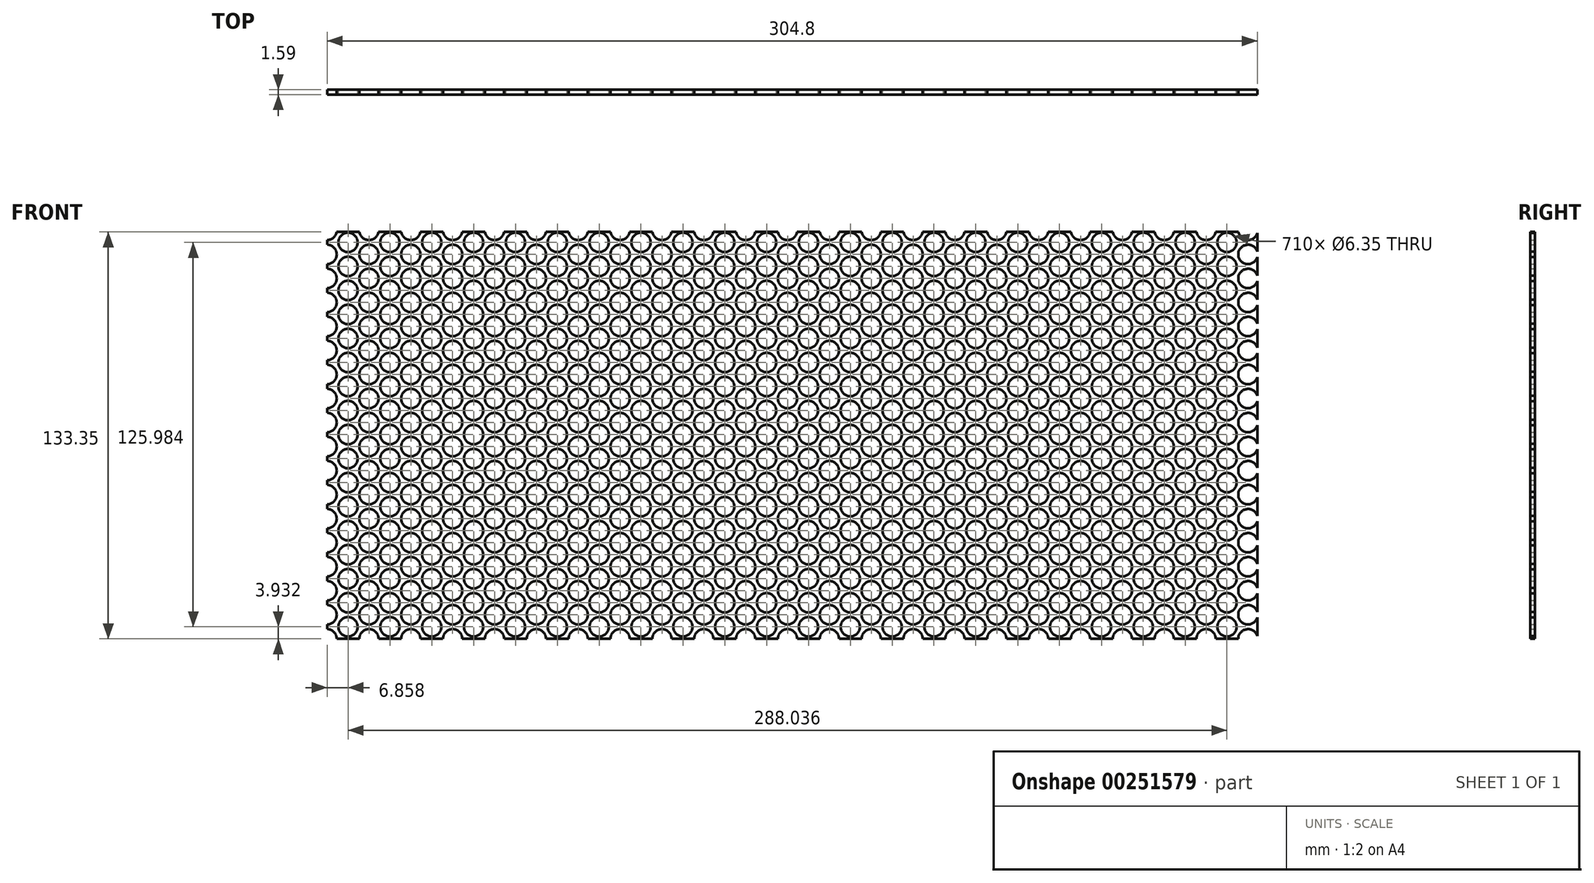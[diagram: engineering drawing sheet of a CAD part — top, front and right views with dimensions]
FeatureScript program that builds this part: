
annotation { "Feature Type Name" : "Feature", "Feature Type Description" : "" }
export const myFeature = defineFeature(function(context is Context, id is Id, definition is map)
    precondition{}
    {
        {
            var Q0;
            Q0=qCreatedBy(makeId("Front.planeOp"),FACE);
            var sketch = newSketch(context, id + "F0", { "sketchPlane" : qUnion([Q0])});
            skLineSegment(sketch, "E0.bottom", {"start": v(-127, 47.63) * mm, "end": v(177.8, 47.63) * mm});
            skLineSegment(sketch, "E0.top", {"start": v(-127, -85.73) * mm, "end": v(177.8, -85.73) * mm});
            skLineSegment(sketch, "E0.left", {"start": v(-127, 47.63) * mm, "end": v(-127, -85.73) * mm});
            skLineSegment(sketch, "E0.right", {"start": v(177.8, 47.63) * mm, "end": v(177.8, -85.73) * mm});
            skPoint(sketch, "E1", {"position": v(-127, -85.73) * mm});
            skPoint(sketch, "E2", {"position": v(-120.14, -81.79) * mm});
            skPoint(sketch, "E3.0.1.0", {"position": v(-127, -77.85) * mm});
            skPoint(sketch, "E3.0.1.1", {"position": v(-120.14, -73.91) * mm});
            skPoint(sketch, "E3.0.2.0", {"position": v(-127, -69.98) * mm});
            skPoint(sketch, "E3.0.2.1", {"position": v(-120.14, -66.04) * mm});
            skPoint(sketch, "E3.0.3.0", {"position": v(-127, -62.1) * mm});
            skPoint(sketch, "E3.0.3.1", {"position": v(-120.14, -58.17) * mm});
            skPoint(sketch, "E3.0.4.0", {"position": v(-127, -54.23) * mm});
            skPoint(sketch, "E3.0.4.1", {"position": v(-120.14, -50.3) * mm});
            skPoint(sketch, "E3.0.5.0", {"position": v(-127, -46.35) * mm});
            skPoint(sketch, "E3.0.5.1", {"position": v(-120.14, -42.42) * mm});
            skPoint(sketch, "E3.0.6.0", {"position": v(-127, -38.48) * mm});
            skPoint(sketch, "E3.0.6.1", {"position": v(-120.14, -34.54) * mm});
            skPoint(sketch, "E3.0.7.0", {"position": v(-127, -30.6) * mm});
            skPoint(sketch, "E3.0.7.1", {"position": v(-120.14, -26.67) * mm});
            skPoint(sketch, "E3.0.8.0", {"position": v(-127, -22.73) * mm});
            skPoint(sketch, "E3.0.8.1", {"position": v(-120.14, -18.8) * mm});
            skPoint(sketch, "E3.0.9.0", {"position": v(-127, -14.86) * mm});
            skPoint(sketch, "E3.0.9.1", {"position": v(-120.14, -10.92) * mm});
            skPoint(sketch, "E3.0.10.0", {"position": v(-127, -6.98) * mm});
            skPoint(sketch, "E3.0.10.1", {"position": v(-120.14, -3.05) * mm});
            skPoint(sketch, "E3.0.11.0", {"position": v(-127, 0.89) * mm});
            skPoint(sketch, "E3.0.11.1", {"position": v(-120.14, 4.83) * mm});
            skPoint(sketch, "E3.0.12.0", {"position": v(-127, 8.76) * mm});
            skPoint(sketch, "E3.0.12.1", {"position": v(-120.14, 12.7) * mm});
            skPoint(sketch, "E3.0.13.0", {"position": v(-127, 16.64) * mm});
            skPoint(sketch, "E3.0.13.1", {"position": v(-120.14, 20.57) * mm});
            skPoint(sketch, "E3.0.14.0", {"position": v(-127, 24.51) * mm});
            skPoint(sketch, "E3.0.14.1", {"position": v(-120.14, 28.45) * mm});
            skPoint(sketch, "E3.0.15.0", {"position": v(-127, 32.39) * mm});
            skPoint(sketch, "E3.0.15.1", {"position": v(-120.14, 36.32) * mm});
            skPoint(sketch, "E3.0.16.0", {"position": v(-127, 40.26) * mm});
            skPoint(sketch, "E3.0.16.1", {"position": v(-120.14, 44.2) * mm});
            skPoint(sketch, "E3.0.17.0", {"position": v(-127, 48.13) * mm});
            skPoint(sketch, "E3.0.17.1", {"position": v(-120.14, 52.07) * mm});
            skPoint(sketch, "E3.1.0.0", {"position": v(-113.28, -85.73) * mm});
            skPoint(sketch, "E3.1.0.1", {"position": v(-106.43, -81.79) * mm});
            skPoint(sketch, "E3.1.1.0", {"position": v(-113.28, -77.85) * mm});
            skPoint(sketch, "E3.1.1.1", {"position": v(-106.43, -73.91) * mm});
            skPoint(sketch, "E3.1.2.0", {"position": v(-113.28, -69.98) * mm});
            skPoint(sketch, "E3.1.2.1", {"position": v(-106.43, -66.04) * mm});
            skPoint(sketch, "E3.1.3.0", {"position": v(-113.28, -62.1) * mm});
            skPoint(sketch, "E3.1.3.1", {"position": v(-106.43, -58.17) * mm});
            skPoint(sketch, "E3.1.4.0", {"position": v(-113.28, -54.23) * mm});
            skPoint(sketch, "E3.1.4.1", {"position": v(-106.43, -50.3) * mm});
            skPoint(sketch, "E3.1.5.0", {"position": v(-113.28, -46.35) * mm});
            skPoint(sketch, "E3.1.5.1", {"position": v(-106.43, -42.42) * mm});
            skPoint(sketch, "E3.1.6.0", {"position": v(-113.28, -38.48) * mm});
            skPoint(sketch, "E3.1.6.1", {"position": v(-106.43, -34.54) * mm});
            skPoint(sketch, "E3.1.7.0", {"position": v(-113.28, -30.6) * mm});
            skPoint(sketch, "E3.1.7.1", {"position": v(-106.43, -26.67) * mm});
            skPoint(sketch, "E3.1.8.0", {"position": v(-113.28, -22.73) * mm});
            skPoint(sketch, "E3.1.8.1", {"position": v(-106.43, -18.8) * mm});
            skPoint(sketch, "E3.1.9.0", {"position": v(-113.28, -14.86) * mm});
            skPoint(sketch, "E3.1.9.1", {"position": v(-106.43, -10.92) * mm});
            skPoint(sketch, "E3.1.10.0", {"position": v(-113.28, -6.98) * mm});
            skPoint(sketch, "E3.1.10.1", {"position": v(-106.43, -3.05) * mm});
            skPoint(sketch, "E3.1.11.0", {"position": v(-113.28, 0.89) * mm});
            skPoint(sketch, "E3.1.11.1", {"position": v(-106.43, 4.83) * mm});
            skPoint(sketch, "E3.1.12.0", {"position": v(-113.28, 8.76) * mm});
            skPoint(sketch, "E3.1.12.1", {"position": v(-106.43, 12.7) * mm});
            skPoint(sketch, "E3.1.13.0", {"position": v(-113.28, 16.64) * mm});
            skPoint(sketch, "E3.1.13.1", {"position": v(-106.43, 20.57) * mm});
            skPoint(sketch, "E3.1.14.0", {"position": v(-113.28, 24.51) * mm});
            skPoint(sketch, "E3.1.14.1", {"position": v(-106.43, 28.45) * mm});
            skPoint(sketch, "E3.1.15.0", {"position": v(-113.28, 32.39) * mm});
            skPoint(sketch, "E3.1.15.1", {"position": v(-106.43, 36.32) * mm});
            skPoint(sketch, "E3.1.16.0", {"position": v(-113.28, 40.26) * mm});
            skPoint(sketch, "E3.1.16.1", {"position": v(-106.43, 44.2) * mm});
            skPoint(sketch, "E3.1.17.0", {"position": v(-113.28, 48.13) * mm});
            skPoint(sketch, "E3.1.17.1", {"position": v(-106.43, 52.07) * mm});
            skPoint(sketch, "E3.2.0.0", {"position": v(-99.57, -85.73) * mm});
            skPoint(sketch, "E3.2.0.1", {"position": v(-92.71, -81.79) * mm});
            skPoint(sketch, "E3.2.1.0", {"position": v(-99.57, -77.85) * mm});
            skPoint(sketch, "E3.2.1.1", {"position": v(-92.71, -73.91) * mm});
            skPoint(sketch, "E3.2.2.0", {"position": v(-99.57, -69.98) * mm});
            skPoint(sketch, "E3.2.2.1", {"position": v(-92.71, -66.04) * mm});
            skPoint(sketch, "E3.2.3.0", {"position": v(-99.57, -62.1) * mm});
            skPoint(sketch, "E3.2.3.1", {"position": v(-92.71, -58.17) * mm});
            skPoint(sketch, "E3.2.4.0", {"position": v(-99.57, -54.23) * mm});
            skPoint(sketch, "E3.2.4.1", {"position": v(-92.71, -50.3) * mm});
            skPoint(sketch, "E3.2.5.0", {"position": v(-99.57, -46.35) * mm});
            skPoint(sketch, "E3.2.5.1", {"position": v(-92.71, -42.42) * mm});
            skPoint(sketch, "E3.2.6.0", {"position": v(-99.57, -38.48) * mm});
            skPoint(sketch, "E3.2.6.1", {"position": v(-92.71, -34.54) * mm});
            skPoint(sketch, "E3.2.7.0", {"position": v(-99.57, -30.6) * mm});
            skPoint(sketch, "E3.2.7.1", {"position": v(-92.71, -26.67) * mm});
            skPoint(sketch, "E3.2.8.0", {"position": v(-99.57, -22.73) * mm});
            skPoint(sketch, "E3.2.8.1", {"position": v(-92.71, -18.8) * mm});
            skPoint(sketch, "E3.2.9.0", {"position": v(-99.57, -14.86) * mm});
            skPoint(sketch, "E3.2.9.1", {"position": v(-92.71, -10.92) * mm});
            skPoint(sketch, "E3.2.10.0", {"position": v(-99.57, -6.98) * mm});
            skPoint(sketch, "E3.2.10.1", {"position": v(-92.71, -3.05) * mm});
            skPoint(sketch, "E3.2.11.0", {"position": v(-99.57, 0.89) * mm});
            skPoint(sketch, "E3.2.11.1", {"position": v(-92.71, 4.83) * mm});
            skPoint(sketch, "E3.2.12.0", {"position": v(-99.57, 8.76) * mm});
            skPoint(sketch, "E3.2.12.1", {"position": v(-92.71, 12.7) * mm});
            skPoint(sketch, "E3.2.13.0", {"position": v(-99.57, 16.64) * mm});
            skPoint(sketch, "E3.2.13.1", {"position": v(-92.71, 20.57) * mm});
            skPoint(sketch, "E3.2.14.0", {"position": v(-99.57, 24.51) * mm});
            skPoint(sketch, "E3.2.14.1", {"position": v(-92.71, 28.45) * mm});
            skPoint(sketch, "E3.2.15.0", {"position": v(-99.57, 32.39) * mm});
            skPoint(sketch, "E3.2.15.1", {"position": v(-92.71, 36.32) * mm});
            skPoint(sketch, "E3.2.16.0", {"position": v(-99.57, 40.26) * mm});
            skPoint(sketch, "E3.2.16.1", {"position": v(-92.71, 44.2) * mm});
            skPoint(sketch, "E3.2.17.0", {"position": v(-99.57, 48.13) * mm});
            skPoint(sketch, "E3.2.17.1", {"position": v(-92.71, 52.07) * mm});
            skPoint(sketch, "E3.3.0.0", {"position": v(-85.85, -85.73) * mm});
            skPoint(sketch, "E3.3.0.1", {"position": v(-79, -81.79) * mm});
            skPoint(sketch, "E3.3.1.0", {"position": v(-85.85, -77.85) * mm});
            skPoint(sketch, "E3.3.1.1", {"position": v(-79, -73.91) * mm});
            skPoint(sketch, "E3.3.2.0", {"position": v(-85.85, -69.98) * mm});
            skPoint(sketch, "E3.3.2.1", {"position": v(-79, -66.04) * mm});
            skPoint(sketch, "E3.3.3.0", {"position": v(-85.85, -62.1) * mm});
            skPoint(sketch, "E3.3.3.1", {"position": v(-79, -58.17) * mm});
            skPoint(sketch, "E3.3.4.0", {"position": v(-85.85, -54.23) * mm});
            skPoint(sketch, "E3.3.4.1", {"position": v(-79, -50.3) * mm});
            skPoint(sketch, "E3.3.5.0", {"position": v(-85.85, -46.35) * mm});
            skPoint(sketch, "E3.3.5.1", {"position": v(-79, -42.42) * mm});
            skPoint(sketch, "E3.3.6.0", {"position": v(-85.85, -38.48) * mm});
            skPoint(sketch, "E3.3.6.1", {"position": v(-79, -34.54) * mm});
            skPoint(sketch, "E3.3.7.0", {"position": v(-85.85, -30.6) * mm});
            skPoint(sketch, "E3.3.7.1", {"position": v(-79, -26.67) * mm});
            skPoint(sketch, "E3.3.8.0", {"position": v(-85.85, -22.73) * mm});
            skPoint(sketch, "E3.3.8.1", {"position": v(-79, -18.8) * mm});
            skPoint(sketch, "E3.3.9.0", {"position": v(-85.85, -14.86) * mm});
            skPoint(sketch, "E3.3.9.1", {"position": v(-79, -10.92) * mm});
            skPoint(sketch, "E3.3.10.0", {"position": v(-85.85, -6.98) * mm});
            skPoint(sketch, "E3.3.10.1", {"position": v(-79, -3.05) * mm});
            skPoint(sketch, "E3.3.11.0", {"position": v(-85.85, 0.89) * mm});
            skPoint(sketch, "E3.3.11.1", {"position": v(-79, 4.83) * mm});
            skPoint(sketch, "E3.3.12.0", {"position": v(-85.85, 8.76) * mm});
            skPoint(sketch, "E3.3.12.1", {"position": v(-79, 12.7) * mm});
            skPoint(sketch, "E3.3.13.0", {"position": v(-85.85, 16.64) * mm});
            skPoint(sketch, "E3.3.13.1", {"position": v(-79, 20.57) * mm});
            skPoint(sketch, "E3.3.14.0", {"position": v(-85.85, 24.51) * mm});
            skPoint(sketch, "E3.3.14.1", {"position": v(-79, 28.45) * mm});
            skPoint(sketch, "E3.3.15.0", {"position": v(-85.85, 32.39) * mm});
            skPoint(sketch, "E3.3.15.1", {"position": v(-79, 36.32) * mm});
            skPoint(sketch, "E3.3.16.0", {"position": v(-85.85, 40.26) * mm});
            skPoint(sketch, "E3.3.16.1", {"position": v(-79, 44.2) * mm});
            skPoint(sketch, "E3.3.17.0", {"position": v(-85.85, 48.13) * mm});
            skPoint(sketch, "E3.3.17.1", {"position": v(-79, 52.07) * mm});
            skPoint(sketch, "E3.4.0.0", {"position": v(-72.14, -85.73) * mm});
            skPoint(sketch, "E3.4.0.1", {"position": v(-65.28, -81.79) * mm});
            skPoint(sketch, "E3.4.1.0", {"position": v(-72.14, -77.85) * mm});
            skPoint(sketch, "E3.4.1.1", {"position": v(-65.28, -73.91) * mm});
            skPoint(sketch, "E3.4.2.0", {"position": v(-72.14, -69.98) * mm});
            skPoint(sketch, "E3.4.2.1", {"position": v(-65.28, -66.04) * mm});
            skPoint(sketch, "E3.4.3.0", {"position": v(-72.14, -62.1) * mm});
            skPoint(sketch, "E3.4.3.1", {"position": v(-65.28, -58.17) * mm});
            skPoint(sketch, "E3.4.4.0", {"position": v(-72.14, -54.23) * mm});
            skPoint(sketch, "E3.4.4.1", {"position": v(-65.28, -50.3) * mm});
            skPoint(sketch, "E3.4.5.0", {"position": v(-72.14, -46.35) * mm});
            skPoint(sketch, "E3.4.5.1", {"position": v(-65.28, -42.42) * mm});
            skPoint(sketch, "E3.4.6.0", {"position": v(-72.14, -38.48) * mm});
            skPoint(sketch, "E3.4.6.1", {"position": v(-65.28, -34.54) * mm});
            skPoint(sketch, "E3.4.7.0", {"position": v(-72.14, -30.6) * mm});
            skPoint(sketch, "E3.4.7.1", {"position": v(-65.28, -26.67) * mm});
            skPoint(sketch, "E3.4.8.0", {"position": v(-72.14, -22.73) * mm});
            skPoint(sketch, "E3.4.8.1", {"position": v(-65.28, -18.8) * mm});
            skPoint(sketch, "E3.4.9.0", {"position": v(-72.14, -14.86) * mm});
            skPoint(sketch, "E3.4.9.1", {"position": v(-65.28, -10.92) * mm});
            skPoint(sketch, "E3.4.10.0", {"position": v(-72.14, -6.98) * mm});
            skPoint(sketch, "E3.4.10.1", {"position": v(-65.28, -3.05) * mm});
            skPoint(sketch, "E3.4.11.0", {"position": v(-72.14, 0.89) * mm});
            skPoint(sketch, "E3.4.11.1", {"position": v(-65.28, 4.83) * mm});
            skPoint(sketch, "E3.4.12.0", {"position": v(-72.14, 8.76) * mm});
            skPoint(sketch, "E3.4.12.1", {"position": v(-65.28, 12.7) * mm});
            skPoint(sketch, "E3.4.13.0", {"position": v(-72.14, 16.64) * mm});
            skPoint(sketch, "E3.4.13.1", {"position": v(-65.28, 20.57) * mm});
            skPoint(sketch, "E3.4.14.0", {"position": v(-72.14, 24.51) * mm});
            skPoint(sketch, "E3.4.14.1", {"position": v(-65.28, 28.45) * mm});
            skPoint(sketch, "E3.4.15.0", {"position": v(-72.14, 32.39) * mm});
            skPoint(sketch, "E3.4.15.1", {"position": v(-65.28, 36.32) * mm});
            skPoint(sketch, "E3.4.16.0", {"position": v(-72.14, 40.26) * mm});
            skPoint(sketch, "E3.4.16.1", {"position": v(-65.28, 44.2) * mm});
            skPoint(sketch, "E3.4.17.0", {"position": v(-72.14, 48.13) * mm});
            skPoint(sketch, "E3.4.17.1", {"position": v(-65.28, 52.07) * mm});
            skPoint(sketch, "E3.5.0.0", {"position": v(-58.42, -85.73) * mm});
            skPoint(sketch, "E3.5.0.1", {"position": v(-51.56, -81.79) * mm});
            skPoint(sketch, "E3.5.1.0", {"position": v(-58.42, -77.85) * mm});
            skPoint(sketch, "E3.5.1.1", {"position": v(-51.56, -73.91) * mm});
            skPoint(sketch, "E3.5.2.0", {"position": v(-58.42, -69.98) * mm});
            skPoint(sketch, "E3.5.2.1", {"position": v(-51.56, -66.04) * mm});
            skPoint(sketch, "E3.5.3.0", {"position": v(-58.42, -62.1) * mm});
            skPoint(sketch, "E3.5.3.1", {"position": v(-51.56, -58.17) * mm});
            skPoint(sketch, "E3.5.4.0", {"position": v(-58.42, -54.23) * mm});
            skPoint(sketch, "E3.5.4.1", {"position": v(-51.56, -50.3) * mm});
            skPoint(sketch, "E3.5.5.0", {"position": v(-58.42, -46.35) * mm});
            skPoint(sketch, "E3.5.5.1", {"position": v(-51.56, -42.42) * mm});
            skPoint(sketch, "E3.5.6.0", {"position": v(-58.42, -38.48) * mm});
            skPoint(sketch, "E3.5.6.1", {"position": v(-51.56, -34.54) * mm});
            skPoint(sketch, "E3.5.7.0", {"position": v(-58.42, -30.6) * mm});
            skPoint(sketch, "E3.5.7.1", {"position": v(-51.56, -26.67) * mm});
            skPoint(sketch, "E3.5.8.0", {"position": v(-58.42, -22.73) * mm});
            skPoint(sketch, "E3.5.8.1", {"position": v(-51.56, -18.8) * mm});
            skPoint(sketch, "E3.5.9.0", {"position": v(-58.42, -14.86) * mm});
            skPoint(sketch, "E3.5.9.1", {"position": v(-51.56, -10.92) * mm});
            skPoint(sketch, "E3.5.10.0", {"position": v(-58.42, -6.98) * mm});
            skPoint(sketch, "E3.5.10.1", {"position": v(-51.56, -3.05) * mm});
            skPoint(sketch, "E3.5.11.0", {"position": v(-58.42, 0.89) * mm});
            skPoint(sketch, "E3.5.11.1", {"position": v(-51.56, 4.83) * mm});
            skPoint(sketch, "E3.5.12.0", {"position": v(-58.42, 8.76) * mm});
            skPoint(sketch, "E3.5.12.1", {"position": v(-51.56, 12.7) * mm});
            skPoint(sketch, "E3.5.13.0", {"position": v(-58.42, 16.64) * mm});
            skPoint(sketch, "E3.5.13.1", {"position": v(-51.56, 20.57) * mm});
            skPoint(sketch, "E3.5.14.0", {"position": v(-58.42, 24.51) * mm});
            skPoint(sketch, "E3.5.14.1", {"position": v(-51.56, 28.45) * mm});
            skPoint(sketch, "E3.5.15.0", {"position": v(-58.42, 32.39) * mm});
            skPoint(sketch, "E3.5.15.1", {"position": v(-51.56, 36.32) * mm});
            skPoint(sketch, "E3.5.16.0", {"position": v(-58.42, 40.26) * mm});
            skPoint(sketch, "E3.5.16.1", {"position": v(-51.56, 44.2) * mm});
            skPoint(sketch, "E3.5.17.0", {"position": v(-58.42, 48.13) * mm});
            skPoint(sketch, "E3.5.17.1", {"position": v(-51.56, 52.07) * mm});
            skPoint(sketch, "E3.6.0.0", {"position": v(-44.7, -85.73) * mm});
            skPoint(sketch, "E3.6.0.1", {"position": v(-37.85, -81.79) * mm});
            skPoint(sketch, "E3.6.1.0", {"position": v(-44.7, -77.85) * mm});
            skPoint(sketch, "E3.6.1.1", {"position": v(-37.85, -73.91) * mm});
            skPoint(sketch, "E3.6.2.0", {"position": v(-44.7, -69.98) * mm});
            skPoint(sketch, "E3.6.2.1", {"position": v(-37.85, -66.04) * mm});
            skPoint(sketch, "E3.6.3.0", {"position": v(-44.7, -62.1) * mm});
            skPoint(sketch, "E3.6.3.1", {"position": v(-37.85, -58.17) * mm});
            skPoint(sketch, "E3.6.4.0", {"position": v(-44.7, -54.23) * mm});
            skPoint(sketch, "E3.6.4.1", {"position": v(-37.85, -50.3) * mm});
            skPoint(sketch, "E3.6.5.0", {"position": v(-44.7, -46.35) * mm});
            skPoint(sketch, "E3.6.5.1", {"position": v(-37.85, -42.42) * mm});
            skPoint(sketch, "E3.6.6.0", {"position": v(-44.7, -38.48) * mm});
            skPoint(sketch, "E3.6.6.1", {"position": v(-37.85, -34.54) * mm});
            skPoint(sketch, "E3.6.7.0", {"position": v(-44.7, -30.6) * mm});
            skPoint(sketch, "E3.6.7.1", {"position": v(-37.85, -26.67) * mm});
            skPoint(sketch, "E3.6.8.0", {"position": v(-44.7, -22.73) * mm});
            skPoint(sketch, "E3.6.8.1", {"position": v(-37.85, -18.8) * mm});
            skPoint(sketch, "E3.6.9.0", {"position": v(-44.7, -14.86) * mm});
            skPoint(sketch, "E3.6.9.1", {"position": v(-37.85, -10.92) * mm});
            skPoint(sketch, "E3.6.10.0", {"position": v(-44.7, -6.98) * mm});
            skPoint(sketch, "E3.6.10.1", {"position": v(-37.85, -3.05) * mm});
            skPoint(sketch, "E3.6.11.0", {"position": v(-44.7, 0.89) * mm});
            skPoint(sketch, "E3.6.11.1", {"position": v(-37.85, 4.83) * mm});
            skPoint(sketch, "E3.6.12.0", {"position": v(-44.7, 8.76) * mm});
            skPoint(sketch, "E3.6.12.1", {"position": v(-37.85, 12.7) * mm});
            skPoint(sketch, "E3.6.13.0", {"position": v(-44.7, 16.64) * mm});
            skPoint(sketch, "E3.6.13.1", {"position": v(-37.85, 20.57) * mm});
            skPoint(sketch, "E3.6.14.0", {"position": v(-44.7, 24.51) * mm});
            skPoint(sketch, "E3.6.14.1", {"position": v(-37.85, 28.45) * mm});
            skPoint(sketch, "E3.6.15.0", {"position": v(-44.7, 32.39) * mm});
            skPoint(sketch, "E3.6.15.1", {"position": v(-37.85, 36.32) * mm});
            skPoint(sketch, "E3.6.16.0", {"position": v(-44.7, 40.26) * mm});
            skPoint(sketch, "E3.6.16.1", {"position": v(-37.85, 44.2) * mm});
            skPoint(sketch, "E3.6.17.0", {"position": v(-44.7, 48.13) * mm});
            skPoint(sketch, "E3.6.17.1", {"position": v(-37.85, 52.07) * mm});
            skPoint(sketch, "E3.7.0.0", {"position": v(-30.99, -85.73) * mm});
            skPoint(sketch, "E3.7.0.1", {"position": v(-24.13, -81.79) * mm});
            skPoint(sketch, "E3.7.1.0", {"position": v(-30.99, -77.85) * mm});
            skPoint(sketch, "E3.7.1.1", {"position": v(-24.13, -73.91) * mm});
            skPoint(sketch, "E3.7.2.0", {"position": v(-30.99, -69.98) * mm});
            skPoint(sketch, "E3.7.2.1", {"position": v(-24.13, -66.04) * mm});
            skPoint(sketch, "E3.7.3.0", {"position": v(-30.99, -62.1) * mm});
            skPoint(sketch, "E3.7.3.1", {"position": v(-24.13, -58.17) * mm});
            skPoint(sketch, "E3.7.4.0", {"position": v(-30.99, -54.23) * mm});
            skPoint(sketch, "E3.7.4.1", {"position": v(-24.13, -50.3) * mm});
            skPoint(sketch, "E3.7.5.0", {"position": v(-30.99, -46.35) * mm});
            skPoint(sketch, "E3.7.5.1", {"position": v(-24.13, -42.42) * mm});
            skPoint(sketch, "E3.7.6.0", {"position": v(-30.99, -38.48) * mm});
            skPoint(sketch, "E3.7.6.1", {"position": v(-24.13, -34.54) * mm});
            skPoint(sketch, "E3.7.7.0", {"position": v(-30.99, -30.6) * mm});
            skPoint(sketch, "E3.7.7.1", {"position": v(-24.13, -26.67) * mm});
            skPoint(sketch, "E3.7.8.0", {"position": v(-30.99, -22.73) * mm});
            skPoint(sketch, "E3.7.8.1", {"position": v(-24.13, -18.8) * mm});
            skPoint(sketch, "E3.7.9.0", {"position": v(-30.99, -14.86) * mm});
            skPoint(sketch, "E3.7.9.1", {"position": v(-24.13, -10.92) * mm});
            skPoint(sketch, "E3.7.10.0", {"position": v(-30.99, -6.98) * mm});
            skPoint(sketch, "E3.7.10.1", {"position": v(-24.13, -3.05) * mm});
            skPoint(sketch, "E3.7.11.0", {"position": v(-30.99, 0.89) * mm});
            skPoint(sketch, "E3.7.11.1", {"position": v(-24.13, 4.83) * mm});
            skPoint(sketch, "E3.7.12.0", {"position": v(-30.99, 8.76) * mm});
            skPoint(sketch, "E3.7.12.1", {"position": v(-24.13, 12.7) * mm});
            skPoint(sketch, "E3.7.13.0", {"position": v(-30.99, 16.64) * mm});
            skPoint(sketch, "E3.7.13.1", {"position": v(-24.13, 20.57) * mm});
            skPoint(sketch, "E3.7.14.0", {"position": v(-30.99, 24.51) * mm});
            skPoint(sketch, "E3.7.14.1", {"position": v(-24.13, 28.45) * mm});
            skPoint(sketch, "E3.7.15.0", {"position": v(-30.99, 32.39) * mm});
            skPoint(sketch, "E3.7.15.1", {"position": v(-24.13, 36.32) * mm});
            skPoint(sketch, "E3.7.16.0", {"position": v(-30.99, 40.26) * mm});
            skPoint(sketch, "E3.7.16.1", {"position": v(-24.13, 44.2) * mm});
            skPoint(sketch, "E3.7.17.0", {"position": v(-30.99, 48.13) * mm});
            skPoint(sketch, "E3.7.17.1", {"position": v(-24.13, 52.07) * mm});
            skPoint(sketch, "E3.8.0.0", {"position": v(-17.27, -85.73) * mm});
            skPoint(sketch, "E3.8.0.1", {"position": v(-10.41, -81.79) * mm});
            skPoint(sketch, "E3.8.1.0", {"position": v(-17.27, -77.85) * mm});
            skPoint(sketch, "E3.8.1.1", {"position": v(-10.41, -73.91) * mm});
            skPoint(sketch, "E3.8.2.0", {"position": v(-17.27, -69.98) * mm});
            skPoint(sketch, "E3.8.2.1", {"position": v(-10.41, -66.04) * mm});
            skPoint(sketch, "E3.8.3.0", {"position": v(-17.27, -62.1) * mm});
            skPoint(sketch, "E3.8.3.1", {"position": v(-10.41, -58.17) * mm});
            skPoint(sketch, "E3.8.4.0", {"position": v(-17.27, -54.23) * mm});
            skPoint(sketch, "E3.8.4.1", {"position": v(-10.41, -50.3) * mm});
            skPoint(sketch, "E3.8.5.0", {"position": v(-17.27, -46.35) * mm});
            skPoint(sketch, "E3.8.5.1", {"position": v(-10.41, -42.42) * mm});
            skPoint(sketch, "E3.8.6.0", {"position": v(-17.27, -38.48) * mm});
            skPoint(sketch, "E3.8.6.1", {"position": v(-10.41, -34.54) * mm});
            skPoint(sketch, "E3.8.7.0", {"position": v(-17.27, -30.6) * mm});
            skPoint(sketch, "E3.8.7.1", {"position": v(-10.41, -26.67) * mm});
            skPoint(sketch, "E3.8.8.0", {"position": v(-17.27, -22.73) * mm});
            skPoint(sketch, "E3.8.8.1", {"position": v(-10.41, -18.8) * mm});
            skPoint(sketch, "E3.8.9.0", {"position": v(-17.27, -14.86) * mm});
            skPoint(sketch, "E3.8.9.1", {"position": v(-10.41, -10.92) * mm});
            skPoint(sketch, "E3.8.10.0", {"position": v(-17.27, -6.98) * mm});
            skPoint(sketch, "E3.8.10.1", {"position": v(-10.41, -3.05) * mm});
            skPoint(sketch, "E3.8.11.0", {"position": v(-17.27, 0.89) * mm});
            skPoint(sketch, "E3.8.11.1", {"position": v(-10.41, 4.83) * mm});
            skPoint(sketch, "E3.8.12.0", {"position": v(-17.27, 8.76) * mm});
            skPoint(sketch, "E3.8.12.1", {"position": v(-10.41, 12.7) * mm});
            skPoint(sketch, "E3.8.13.0", {"position": v(-17.27, 16.64) * mm});
            skPoint(sketch, "E3.8.13.1", {"position": v(-10.41, 20.57) * mm});
            skPoint(sketch, "E3.8.14.0", {"position": v(-17.27, 24.51) * mm});
            skPoint(sketch, "E3.8.14.1", {"position": v(-10.41, 28.45) * mm});
            skPoint(sketch, "E3.8.15.0", {"position": v(-17.27, 32.39) * mm});
            skPoint(sketch, "E3.8.15.1", {"position": v(-10.41, 36.32) * mm});
            skPoint(sketch, "E3.8.16.0", {"position": v(-17.27, 40.26) * mm});
            skPoint(sketch, "E3.8.16.1", {"position": v(-10.41, 44.2) * mm});
            skPoint(sketch, "E3.8.17.0", {"position": v(-17.27, 48.13) * mm});
            skPoint(sketch, "E3.8.17.1", {"position": v(-10.41, 52.07) * mm});
            skPoint(sketch, "E3.9.0.0", {"position": v(-3.56, -85.73) * mm});
            skPoint(sketch, "E3.9.0.1", {"position": v(3.3, -81.79) * mm});
            skPoint(sketch, "E3.9.1.0", {"position": v(-3.56, -77.85) * mm});
            skPoint(sketch, "E3.9.1.1", {"position": v(3.3, -73.91) * mm});
            skPoint(sketch, "E3.9.2.0", {"position": v(-3.56, -69.98) * mm});
            skPoint(sketch, "E3.9.2.1", {"position": v(3.3, -66.04) * mm});
            skPoint(sketch, "E3.9.3.0", {"position": v(-3.56, -62.1) * mm});
            skPoint(sketch, "E3.9.3.1", {"position": v(3.3, -58.17) * mm});
            skPoint(sketch, "E3.9.4.0", {"position": v(-3.56, -54.23) * mm});
            skPoint(sketch, "E3.9.4.1", {"position": v(3.3, -50.3) * mm});
            skPoint(sketch, "E3.9.5.0", {"position": v(-3.56, -46.35) * mm});
            skPoint(sketch, "E3.9.5.1", {"position": v(3.3, -42.42) * mm});
            skPoint(sketch, "E3.9.6.0", {"position": v(-3.56, -38.48) * mm});
            skPoint(sketch, "E3.9.6.1", {"position": v(3.3, -34.54) * mm});
            skPoint(sketch, "E3.9.7.0", {"position": v(-3.56, -30.6) * mm});
            skPoint(sketch, "E3.9.7.1", {"position": v(3.3, -26.67) * mm});
            skPoint(sketch, "E3.9.8.0", {"position": v(-3.56, -22.73) * mm});
            skPoint(sketch, "E3.9.8.1", {"position": v(3.3, -18.8) * mm});
            skPoint(sketch, "E3.9.9.0", {"position": v(-3.56, -14.86) * mm});
            skPoint(sketch, "E3.9.9.1", {"position": v(3.3, -10.92) * mm});
            skPoint(sketch, "E3.9.10.0", {"position": v(-3.56, -6.98) * mm});
            skPoint(sketch, "E3.9.10.1", {"position": v(3.3, -3.05) * mm});
            skPoint(sketch, "E3.9.11.0", {"position": v(-3.56, 0.89) * mm});
            skPoint(sketch, "E3.9.11.1", {"position": v(3.3, 4.83) * mm});
            skPoint(sketch, "E3.9.12.0", {"position": v(-3.56, 8.76) * mm});
            skPoint(sketch, "E3.9.12.1", {"position": v(3.3, 12.7) * mm});
            skPoint(sketch, "E3.9.13.0", {"position": v(-3.56, 16.64) * mm});
            skPoint(sketch, "E3.9.13.1", {"position": v(3.3, 20.57) * mm});
            skPoint(sketch, "E3.9.14.0", {"position": v(-3.56, 24.51) * mm});
            skPoint(sketch, "E3.9.14.1", {"position": v(3.3, 28.45) * mm});
            skPoint(sketch, "E3.9.15.0", {"position": v(-3.56, 32.39) * mm});
            skPoint(sketch, "E3.9.15.1", {"position": v(3.3, 36.32) * mm});
            skPoint(sketch, "E3.9.16.0", {"position": v(-3.56, 40.26) * mm});
            skPoint(sketch, "E3.9.16.1", {"position": v(3.3, 44.2) * mm});
            skPoint(sketch, "E3.9.17.0", {"position": v(-3.56, 48.13) * mm});
            skPoint(sketch, "E3.9.17.1", {"position": v(3.3, 52.07) * mm});
            skPoint(sketch, "E3.10.0.0", {"position": v(10.16, -85.73) * mm});
            skPoint(sketch, "E3.10.0.1", {"position": v(17.02, -81.79) * mm});
            skPoint(sketch, "E3.10.1.0", {"position": v(10.16, -77.85) * mm});
            skPoint(sketch, "E3.10.1.1", {"position": v(17.02, -73.91) * mm});
            skPoint(sketch, "E3.10.2.0", {"position": v(10.16, -69.98) * mm});
            skPoint(sketch, "E3.10.2.1", {"position": v(17.02, -66.04) * mm});
            skPoint(sketch, "E3.10.3.0", {"position": v(10.16, -62.1) * mm});
            skPoint(sketch, "E3.10.3.1", {"position": v(17.02, -58.17) * mm});
            skPoint(sketch, "E3.10.4.0", {"position": v(10.16, -54.23) * mm});
            skPoint(sketch, "E3.10.4.1", {"position": v(17.02, -50.3) * mm});
            skPoint(sketch, "E3.10.5.0", {"position": v(10.16, -46.35) * mm});
            skPoint(sketch, "E3.10.5.1", {"position": v(17.02, -42.42) * mm});
            skPoint(sketch, "E3.10.6.0", {"position": v(10.16, -38.48) * mm});
            skPoint(sketch, "E3.10.6.1", {"position": v(17.02, -34.54) * mm});
            skPoint(sketch, "E3.10.7.0", {"position": v(10.16, -30.6) * mm});
            skPoint(sketch, "E3.10.7.1", {"position": v(17.02, -26.67) * mm});
            skPoint(sketch, "E3.10.8.0", {"position": v(10.16, -22.73) * mm});
            skPoint(sketch, "E3.10.8.1", {"position": v(17.02, -18.8) * mm});
            skPoint(sketch, "E3.10.9.0", {"position": v(10.16, -14.86) * mm});
            skPoint(sketch, "E3.10.9.1", {"position": v(17.02, -10.92) * mm});
            skPoint(sketch, "E3.10.10.0", {"position": v(10.16, -6.98) * mm});
            skPoint(sketch, "E3.10.10.1", {"position": v(17.02, -3.05) * mm});
            skPoint(sketch, "E3.10.11.0", {"position": v(10.16, 0.89) * mm});
            skPoint(sketch, "E3.10.11.1", {"position": v(17.02, 4.83) * mm});
            skPoint(sketch, "E3.10.12.0", {"position": v(10.16, 8.76) * mm});
            skPoint(sketch, "E3.10.12.1", {"position": v(17.02, 12.7) * mm});
            skPoint(sketch, "E3.10.13.0", {"position": v(10.16, 16.64) * mm});
            skPoint(sketch, "E3.10.13.1", {"position": v(17.02, 20.57) * mm});
            skPoint(sketch, "E3.10.14.0", {"position": v(10.16, 24.51) * mm});
            skPoint(sketch, "E3.10.14.1", {"position": v(17.02, 28.45) * mm});
            skPoint(sketch, "E3.10.15.0", {"position": v(10.16, 32.39) * mm});
            skPoint(sketch, "E3.10.15.1", {"position": v(17.02, 36.32) * mm});
            skPoint(sketch, "E3.10.16.0", {"position": v(10.16, 40.26) * mm});
            skPoint(sketch, "E3.10.16.1", {"position": v(17.02, 44.2) * mm});
            skPoint(sketch, "E3.10.17.0", {"position": v(10.16, 48.13) * mm});
            skPoint(sketch, "E3.10.17.1", {"position": v(17.02, 52.07) * mm});
            skPoint(sketch, "E3.11.0.0", {"position": v(23.88, -85.73) * mm});
            skPoint(sketch, "E3.11.0.1", {"position": v(30.73, -81.79) * mm});
            skPoint(sketch, "E3.11.1.0", {"position": v(23.88, -77.85) * mm});
            skPoint(sketch, "E3.11.1.1", {"position": v(30.73, -73.91) * mm});
            skPoint(sketch, "E3.11.2.0", {"position": v(23.88, -69.98) * mm});
            skPoint(sketch, "E3.11.2.1", {"position": v(30.73, -66.04) * mm});
            skPoint(sketch, "E3.11.3.0", {"position": v(23.88, -62.1) * mm});
            skPoint(sketch, "E3.11.3.1", {"position": v(30.73, -58.17) * mm});
            skPoint(sketch, "E3.11.4.0", {"position": v(23.88, -54.23) * mm});
            skPoint(sketch, "E3.11.4.1", {"position": v(30.73, -50.3) * mm});
            skPoint(sketch, "E3.11.5.0", {"position": v(23.88, -46.35) * mm});
            skPoint(sketch, "E3.11.5.1", {"position": v(30.73, -42.42) * mm});
            skPoint(sketch, "E3.11.6.0", {"position": v(23.88, -38.48) * mm});
            skPoint(sketch, "E3.11.6.1", {"position": v(30.73, -34.54) * mm});
            skPoint(sketch, "E3.11.7.0", {"position": v(23.88, -30.6) * mm});
            skPoint(sketch, "E3.11.7.1", {"position": v(30.73, -26.67) * mm});
            skPoint(sketch, "E3.11.8.0", {"position": v(23.88, -22.73) * mm});
            skPoint(sketch, "E3.11.8.1", {"position": v(30.73, -18.8) * mm});
            skPoint(sketch, "E3.11.9.0", {"position": v(23.88, -14.86) * mm});
            skPoint(sketch, "E3.11.9.1", {"position": v(30.73, -10.92) * mm});
            skPoint(sketch, "E3.11.10.0", {"position": v(23.88, -6.98) * mm});
            skPoint(sketch, "E3.11.10.1", {"position": v(30.73, -3.05) * mm});
            skPoint(sketch, "E3.11.11.0", {"position": v(23.88, 0.89) * mm});
            skPoint(sketch, "E3.11.11.1", {"position": v(30.73, 4.83) * mm});
            skPoint(sketch, "E3.11.12.0", {"position": v(23.88, 8.76) * mm});
            skPoint(sketch, "E3.11.12.1", {"position": v(30.73, 12.7) * mm});
            skPoint(sketch, "E3.11.13.0", {"position": v(23.88, 16.64) * mm});
            skPoint(sketch, "E3.11.13.1", {"position": v(30.73, 20.57) * mm});
            skPoint(sketch, "E3.11.14.0", {"position": v(23.88, 24.51) * mm});
            skPoint(sketch, "E3.11.14.1", {"position": v(30.73, 28.45) * mm});
            skPoint(sketch, "E3.11.15.0", {"position": v(23.88, 32.39) * mm});
            skPoint(sketch, "E3.11.15.1", {"position": v(30.73, 36.32) * mm});
            skPoint(sketch, "E3.11.16.0", {"position": v(23.88, 40.26) * mm});
            skPoint(sketch, "E3.11.16.1", {"position": v(30.73, 44.2) * mm});
            skPoint(sketch, "E3.11.17.0", {"position": v(23.88, 48.13) * mm});
            skPoint(sketch, "E3.11.17.1", {"position": v(30.73, 52.07) * mm});
            skPoint(sketch, "E3.12.0.0", {"position": v(37.6, -85.73) * mm});
            skPoint(sketch, "E3.12.0.1", {"position": v(44.45, -81.79) * mm});
            skPoint(sketch, "E3.12.1.0", {"position": v(37.6, -77.85) * mm});
            skPoint(sketch, "E3.12.1.1", {"position": v(44.45, -73.91) * mm});
            skPoint(sketch, "E3.12.2.0", {"position": v(37.6, -69.98) * mm});
            skPoint(sketch, "E3.12.2.1", {"position": v(44.45, -66.04) * mm});
            skPoint(sketch, "E3.12.3.0", {"position": v(37.6, -62.1) * mm});
            skPoint(sketch, "E3.12.3.1", {"position": v(44.45, -58.17) * mm});
            skPoint(sketch, "E3.12.4.0", {"position": v(37.6, -54.23) * mm});
            skPoint(sketch, "E3.12.4.1", {"position": v(44.45, -50.3) * mm});
            skPoint(sketch, "E3.12.5.0", {"position": v(37.6, -46.35) * mm});
            skPoint(sketch, "E3.12.5.1", {"position": v(44.45, -42.42) * mm});
            skPoint(sketch, "E3.12.6.0", {"position": v(37.6, -38.48) * mm});
            skPoint(sketch, "E3.12.6.1", {"position": v(44.45, -34.54) * mm});
            skPoint(sketch, "E3.12.7.0", {"position": v(37.6, -30.6) * mm});
            skPoint(sketch, "E3.12.7.1", {"position": v(44.45, -26.67) * mm});
            skPoint(sketch, "E3.12.8.0", {"position": v(37.6, -22.73) * mm});
            skPoint(sketch, "E3.12.8.1", {"position": v(44.45, -18.8) * mm});
            skPoint(sketch, "E3.12.9.0", {"position": v(37.6, -14.86) * mm});
            skPoint(sketch, "E3.12.9.1", {"position": v(44.45, -10.92) * mm});
            skPoint(sketch, "E3.12.10.0", {"position": v(37.6, -6.98) * mm});
            skPoint(sketch, "E3.12.10.1", {"position": v(44.45, -3.05) * mm});
            skPoint(sketch, "E3.12.11.0", {"position": v(37.6, 0.89) * mm});
            skPoint(sketch, "E3.12.11.1", {"position": v(44.45, 4.83) * mm});
            skPoint(sketch, "E3.12.12.0", {"position": v(37.6, 8.76) * mm});
            skPoint(sketch, "E3.12.12.1", {"position": v(44.45, 12.7) * mm});
            skPoint(sketch, "E3.12.13.0", {"position": v(37.6, 16.64) * mm});
            skPoint(sketch, "E3.12.13.1", {"position": v(44.45, 20.57) * mm});
            skPoint(sketch, "E3.12.14.0", {"position": v(37.6, 24.51) * mm});
            skPoint(sketch, "E3.12.14.1", {"position": v(44.45, 28.45) * mm});
            skPoint(sketch, "E3.12.15.0", {"position": v(37.6, 32.39) * mm});
            skPoint(sketch, "E3.12.15.1", {"position": v(44.45, 36.32) * mm});
            skPoint(sketch, "E3.12.16.0", {"position": v(37.6, 40.26) * mm});
            skPoint(sketch, "E3.12.16.1", {"position": v(44.45, 44.2) * mm});
            skPoint(sketch, "E3.12.17.0", {"position": v(37.6, 48.13) * mm});
            skPoint(sketch, "E3.12.17.1", {"position": v(44.45, 52.07) * mm});
            skPoint(sketch, "E3.13.0.0", {"position": v(51.3, -85.73) * mm});
            skPoint(sketch, "E3.13.0.1", {"position": v(58.17, -81.79) * mm});
            skPoint(sketch, "E3.13.1.0", {"position": v(51.3, -77.85) * mm});
            skPoint(sketch, "E3.13.1.1", {"position": v(58.17, -73.91) * mm});
            skPoint(sketch, "E3.13.2.0", {"position": v(51.3, -69.98) * mm});
            skPoint(sketch, "E3.13.2.1", {"position": v(58.17, -66.04) * mm});
            skPoint(sketch, "E3.13.3.0", {"position": v(51.3, -62.1) * mm});
            skPoint(sketch, "E3.13.3.1", {"position": v(58.17, -58.17) * mm});
            skPoint(sketch, "E3.13.4.0", {"position": v(51.3, -54.23) * mm});
            skPoint(sketch, "E3.13.4.1", {"position": v(58.17, -50.3) * mm});
            skPoint(sketch, "E3.13.5.0", {"position": v(51.3, -46.35) * mm});
            skPoint(sketch, "E3.13.5.1", {"position": v(58.17, -42.42) * mm});
            skPoint(sketch, "E3.13.6.0", {"position": v(51.3, -38.48) * mm});
            skPoint(sketch, "E3.13.6.1", {"position": v(58.17, -34.54) * mm});
            skPoint(sketch, "E3.13.7.0", {"position": v(51.3, -30.6) * mm});
            skPoint(sketch, "E3.13.7.1", {"position": v(58.17, -26.67) * mm});
            skPoint(sketch, "E3.13.8.0", {"position": v(51.3, -22.73) * mm});
            skPoint(sketch, "E3.13.8.1", {"position": v(58.17, -18.8) * mm});
            skPoint(sketch, "E3.13.9.0", {"position": v(51.3, -14.86) * mm});
            skPoint(sketch, "E3.13.9.1", {"position": v(58.17, -10.92) * mm});
            skPoint(sketch, "E3.13.10.0", {"position": v(51.3, -6.98) * mm});
            skPoint(sketch, "E3.13.10.1", {"position": v(58.17, -3.05) * mm});
            skPoint(sketch, "E3.13.11.0", {"position": v(51.3, 0.89) * mm});
            skPoint(sketch, "E3.13.11.1", {"position": v(58.17, 4.83) * mm});
            skPoint(sketch, "E3.13.12.0", {"position": v(51.3, 8.76) * mm});
            skPoint(sketch, "E3.13.12.1", {"position": v(58.17, 12.7) * mm});
            skPoint(sketch, "E3.13.13.0", {"position": v(51.3, 16.64) * mm});
            skPoint(sketch, "E3.13.13.1", {"position": v(58.17, 20.57) * mm});
            skPoint(sketch, "E3.13.14.0", {"position": v(51.3, 24.51) * mm});
            skPoint(sketch, "E3.13.14.1", {"position": v(58.17, 28.45) * mm});
            skPoint(sketch, "E3.13.15.0", {"position": v(51.3, 32.39) * mm});
            skPoint(sketch, "E3.13.15.1", {"position": v(58.17, 36.32) * mm});
            skPoint(sketch, "E3.13.16.0", {"position": v(51.3, 40.26) * mm});
            skPoint(sketch, "E3.13.16.1", {"position": v(58.17, 44.2) * mm});
            skPoint(sketch, "E3.13.17.0", {"position": v(51.3, 48.13) * mm});
            skPoint(sketch, "E3.13.17.1", {"position": v(58.17, 52.07) * mm});
            skPoint(sketch, "E3.14.0.0", {"position": v(65.02, -85.73) * mm});
            skPoint(sketch, "E3.14.0.1", {"position": v(71.88, -81.79) * mm});
            skPoint(sketch, "E3.14.1.0", {"position": v(65.02, -77.85) * mm});
            skPoint(sketch, "E3.14.1.1", {"position": v(71.88, -73.91) * mm});
            skPoint(sketch, "E3.14.2.0", {"position": v(65.02, -69.98) * mm});
            skPoint(sketch, "E3.14.2.1", {"position": v(71.88, -66.04) * mm});
            skPoint(sketch, "E3.14.3.0", {"position": v(65.02, -62.1) * mm});
            skPoint(sketch, "E3.14.3.1", {"position": v(71.88, -58.17) * mm});
            skPoint(sketch, "E3.14.4.0", {"position": v(65.02, -54.23) * mm});
            skPoint(sketch, "E3.14.4.1", {"position": v(71.88, -50.3) * mm});
            skPoint(sketch, "E3.14.5.0", {"position": v(65.02, -46.35) * mm});
            skPoint(sketch, "E3.14.5.1", {"position": v(71.88, -42.42) * mm});
            skPoint(sketch, "E3.14.6.0", {"position": v(65.02, -38.48) * mm});
            skPoint(sketch, "E3.14.6.1", {"position": v(71.88, -34.54) * mm});
            skPoint(sketch, "E3.14.7.0", {"position": v(65.02, -30.6) * mm});
            skPoint(sketch, "E3.14.7.1", {"position": v(71.88, -26.67) * mm});
            skPoint(sketch, "E3.14.8.0", {"position": v(65.02, -22.73) * mm});
            skPoint(sketch, "E3.14.8.1", {"position": v(71.88, -18.8) * mm});
            skPoint(sketch, "E3.14.9.0", {"position": v(65.02, -14.86) * mm});
            skPoint(sketch, "E3.14.9.1", {"position": v(71.88, -10.92) * mm});
            skPoint(sketch, "E3.14.10.0", {"position": v(65.02, -6.98) * mm});
            skPoint(sketch, "E3.14.10.1", {"position": v(71.88, -3.05) * mm});
            skPoint(sketch, "E3.14.11.0", {"position": v(65.02, 0.89) * mm});
            skPoint(sketch, "E3.14.11.1", {"position": v(71.88, 4.83) * mm});
            skPoint(sketch, "E3.14.12.0", {"position": v(65.02, 8.76) * mm});
            skPoint(sketch, "E3.14.12.1", {"position": v(71.88, 12.7) * mm});
            skPoint(sketch, "E3.14.13.0", {"position": v(65.02, 16.64) * mm});
            skPoint(sketch, "E3.14.13.1", {"position": v(71.88, 20.57) * mm});
            skPoint(sketch, "E3.14.14.0", {"position": v(65.02, 24.51) * mm});
            skPoint(sketch, "E3.14.14.1", {"position": v(71.88, 28.45) * mm});
            skPoint(sketch, "E3.14.15.0", {"position": v(65.02, 32.39) * mm});
            skPoint(sketch, "E3.14.15.1", {"position": v(71.88, 36.32) * mm});
            skPoint(sketch, "E3.14.16.0", {"position": v(65.02, 40.26) * mm});
            skPoint(sketch, "E3.14.16.1", {"position": v(71.88, 44.2) * mm});
            skPoint(sketch, "E3.14.17.0", {"position": v(65.02, 48.13) * mm});
            skPoint(sketch, "E3.14.17.1", {"position": v(71.88, 52.07) * mm});
            skPoint(sketch, "E3.15.0.0", {"position": v(78.74, -85.73) * mm});
            skPoint(sketch, "E3.15.0.1", {"position": v(85.6, -81.79) * mm});
            skPoint(sketch, "E3.15.1.0", {"position": v(78.74, -77.85) * mm});
            skPoint(sketch, "E3.15.1.1", {"position": v(85.6, -73.91) * mm});
            skPoint(sketch, "E3.15.2.0", {"position": v(78.74, -69.98) * mm});
            skPoint(sketch, "E3.15.2.1", {"position": v(85.6, -66.04) * mm});
            skPoint(sketch, "E3.15.3.0", {"position": v(78.74, -62.1) * mm});
            skPoint(sketch, "E3.15.3.1", {"position": v(85.6, -58.17) * mm});
            skPoint(sketch, "E3.15.4.0", {"position": v(78.74, -54.23) * mm});
            skPoint(sketch, "E3.15.4.1", {"position": v(85.6, -50.3) * mm});
            skPoint(sketch, "E3.15.5.0", {"position": v(78.74, -46.35) * mm});
            skPoint(sketch, "E3.15.5.1", {"position": v(85.6, -42.42) * mm});
            skPoint(sketch, "E3.15.6.0", {"position": v(78.74, -38.48) * mm});
            skPoint(sketch, "E3.15.6.1", {"position": v(85.6, -34.54) * mm});
            skPoint(sketch, "E3.15.7.0", {"position": v(78.74, -30.6) * mm});
            skPoint(sketch, "E3.15.7.1", {"position": v(85.6, -26.67) * mm});
            skPoint(sketch, "E3.15.8.0", {"position": v(78.74, -22.73) * mm});
            skPoint(sketch, "E3.15.8.1", {"position": v(85.6, -18.8) * mm});
            skPoint(sketch, "E3.15.9.0", {"position": v(78.74, -14.86) * mm});
            skPoint(sketch, "E3.15.9.1", {"position": v(85.6, -10.92) * mm});
            skPoint(sketch, "E3.15.10.0", {"position": v(78.74, -6.98) * mm});
            skPoint(sketch, "E3.15.10.1", {"position": v(85.6, -3.05) * mm});
            skPoint(sketch, "E3.15.11.0", {"position": v(78.74, 0.89) * mm});
            skPoint(sketch, "E3.15.11.1", {"position": v(85.6, 4.83) * mm});
            skPoint(sketch, "E3.15.12.0", {"position": v(78.74, 8.76) * mm});
            skPoint(sketch, "E3.15.12.1", {"position": v(85.6, 12.7) * mm});
            skPoint(sketch, "E3.15.13.0", {"position": v(78.74, 16.64) * mm});
            skPoint(sketch, "E3.15.13.1", {"position": v(85.6, 20.57) * mm});
            skPoint(sketch, "E3.15.14.0", {"position": v(78.74, 24.51) * mm});
            skPoint(sketch, "E3.15.14.1", {"position": v(85.6, 28.45) * mm});
            skPoint(sketch, "E3.15.15.0", {"position": v(78.74, 32.39) * mm});
            skPoint(sketch, "E3.15.15.1", {"position": v(85.6, 36.32) * mm});
            skPoint(sketch, "E3.15.16.0", {"position": v(78.74, 40.26) * mm});
            skPoint(sketch, "E3.15.16.1", {"position": v(85.6, 44.2) * mm});
            skPoint(sketch, "E3.15.17.0", {"position": v(78.74, 48.13) * mm});
            skPoint(sketch, "E3.15.17.1", {"position": v(85.6, 52.07) * mm});
            skPoint(sketch, "E3.16.0.0", {"position": v(92.46, -85.73) * mm});
            skPoint(sketch, "E3.16.0.1", {"position": v(99.31, -81.79) * mm});
            skPoint(sketch, "E3.16.1.0", {"position": v(92.46, -77.85) * mm});
            skPoint(sketch, "E3.16.1.1", {"position": v(99.31, -73.91) * mm});
            skPoint(sketch, "E3.16.2.0", {"position": v(92.46, -69.98) * mm});
            skPoint(sketch, "E3.16.2.1", {"position": v(99.31, -66.04) * mm});
            skPoint(sketch, "E3.16.3.0", {"position": v(92.46, -62.1) * mm});
            skPoint(sketch, "E3.16.3.1", {"position": v(99.31, -58.17) * mm});
            skPoint(sketch, "E3.16.4.0", {"position": v(92.46, -54.23) * mm});
            skPoint(sketch, "E3.16.4.1", {"position": v(99.31, -50.3) * mm});
            skPoint(sketch, "E3.16.5.0", {"position": v(92.46, -46.35) * mm});
            skPoint(sketch, "E3.16.5.1", {"position": v(99.31, -42.42) * mm});
            skPoint(sketch, "E3.16.6.0", {"position": v(92.46, -38.48) * mm});
            skPoint(sketch, "E3.16.6.1", {"position": v(99.31, -34.54) * mm});
            skPoint(sketch, "E3.16.7.0", {"position": v(92.46, -30.6) * mm});
            skPoint(sketch, "E3.16.7.1", {"position": v(99.31, -26.67) * mm});
            skPoint(sketch, "E3.16.8.0", {"position": v(92.46, -22.73) * mm});
            skPoint(sketch, "E3.16.8.1", {"position": v(99.31, -18.8) * mm});
            skPoint(sketch, "E3.16.9.0", {"position": v(92.46, -14.86) * mm});
            skPoint(sketch, "E3.16.9.1", {"position": v(99.31, -10.92) * mm});
            skPoint(sketch, "E3.16.10.0", {"position": v(92.46, -6.98) * mm});
            skPoint(sketch, "E3.16.10.1", {"position": v(99.31, -3.05) * mm});
            skPoint(sketch, "E3.16.11.0", {"position": v(92.46, 0.89) * mm});
            skPoint(sketch, "E3.16.11.1", {"position": v(99.31, 4.83) * mm});
            skPoint(sketch, "E3.16.12.0", {"position": v(92.46, 8.76) * mm});
            skPoint(sketch, "E3.16.12.1", {"position": v(99.31, 12.7) * mm});
            skPoint(sketch, "E3.16.13.0", {"position": v(92.46, 16.64) * mm});
            skPoint(sketch, "E3.16.13.1", {"position": v(99.31, 20.57) * mm});
            skPoint(sketch, "E3.16.14.0", {"position": v(92.46, 24.51) * mm});
            skPoint(sketch, "E3.16.14.1", {"position": v(99.31, 28.45) * mm});
            skPoint(sketch, "E3.16.15.0", {"position": v(92.46, 32.39) * mm});
            skPoint(sketch, "E3.16.15.1", {"position": v(99.31, 36.32) * mm});
            skPoint(sketch, "E3.16.16.0", {"position": v(92.46, 40.26) * mm});
            skPoint(sketch, "E3.16.16.1", {"position": v(99.31, 44.2) * mm});
            skPoint(sketch, "E3.16.17.0", {"position": v(92.46, 48.13) * mm});
            skPoint(sketch, "E3.16.17.1", {"position": v(99.31, 52.07) * mm});
            skPoint(sketch, "E3.17.0.0", {"position": v(106.17, -85.73) * mm});
            skPoint(sketch, "E3.17.0.1", {"position": v(113.03, -81.79) * mm});
            skPoint(sketch, "E3.17.1.0", {"position": v(106.17, -77.85) * mm});
            skPoint(sketch, "E3.17.1.1", {"position": v(113.03, -73.91) * mm});
            skPoint(sketch, "E3.17.2.0", {"position": v(106.17, -69.98) * mm});
            skPoint(sketch, "E3.17.2.1", {"position": v(113.03, -66.04) * mm});
            skPoint(sketch, "E3.17.3.0", {"position": v(106.17, -62.1) * mm});
            skPoint(sketch, "E3.17.3.1", {"position": v(113.03, -58.17) * mm});
            skPoint(sketch, "E3.17.4.0", {"position": v(106.17, -54.23) * mm});
            skPoint(sketch, "E3.17.4.1", {"position": v(113.03, -50.3) * mm});
            skPoint(sketch, "E3.17.5.0", {"position": v(106.17, -46.35) * mm});
            skPoint(sketch, "E3.17.5.1", {"position": v(113.03, -42.42) * mm});
            skPoint(sketch, "E3.17.6.0", {"position": v(106.17, -38.48) * mm});
            skPoint(sketch, "E3.17.6.1", {"position": v(113.03, -34.54) * mm});
            skPoint(sketch, "E3.17.7.0", {"position": v(106.17, -30.6) * mm});
            skPoint(sketch, "E3.17.7.1", {"position": v(113.03, -26.67) * mm});
            skPoint(sketch, "E3.17.8.0", {"position": v(106.17, -22.73) * mm});
            skPoint(sketch, "E3.17.8.1", {"position": v(113.03, -18.8) * mm});
            skPoint(sketch, "E3.17.9.0", {"position": v(106.17, -14.86) * mm});
            skPoint(sketch, "E3.17.9.1", {"position": v(113.03, -10.92) * mm});
            skPoint(sketch, "E3.17.10.0", {"position": v(106.17, -6.98) * mm});
            skPoint(sketch, "E3.17.10.1", {"position": v(113.03, -3.05) * mm});
            skPoint(sketch, "E3.17.11.0", {"position": v(106.17, 0.89) * mm});
            skPoint(sketch, "E3.17.11.1", {"position": v(113.03, 4.83) * mm});
            skPoint(sketch, "E3.17.12.0", {"position": v(106.17, 8.76) * mm});
            skPoint(sketch, "E3.17.12.1", {"position": v(113.03, 12.7) * mm});
            skPoint(sketch, "E3.17.13.0", {"position": v(106.17, 16.64) * mm});
            skPoint(sketch, "E3.17.13.1", {"position": v(113.03, 20.57) * mm});
            skPoint(sketch, "E3.17.14.0", {"position": v(106.17, 24.51) * mm});
            skPoint(sketch, "E3.17.14.1", {"position": v(113.03, 28.45) * mm});
            skPoint(sketch, "E3.17.15.0", {"position": v(106.17, 32.39) * mm});
            skPoint(sketch, "E3.17.15.1", {"position": v(113.03, 36.32) * mm});
            skPoint(sketch, "E3.17.16.0", {"position": v(106.17, 40.26) * mm});
            skPoint(sketch, "E3.17.16.1", {"position": v(113.03, 44.2) * mm});
            skPoint(sketch, "E3.17.17.0", {"position": v(106.17, 48.13) * mm});
            skPoint(sketch, "E3.17.17.1", {"position": v(113.03, 52.07) * mm});
            skPoint(sketch, "E3.18.0.0", {"position": v(119.89, -85.73) * mm});
            skPoint(sketch, "E3.18.0.1", {"position": v(126.75, -81.79) * mm});
            skPoint(sketch, "E3.18.1.0", {"position": v(119.89, -77.85) * mm});
            skPoint(sketch, "E3.18.1.1", {"position": v(126.75, -73.91) * mm});
            skPoint(sketch, "E3.18.2.0", {"position": v(119.89, -69.98) * mm});
            skPoint(sketch, "E3.18.2.1", {"position": v(126.75, -66.04) * mm});
            skPoint(sketch, "E3.18.3.0", {"position": v(119.89, -62.1) * mm});
            skPoint(sketch, "E3.18.3.1", {"position": v(126.75, -58.17) * mm});
            skPoint(sketch, "E3.18.4.0", {"position": v(119.89, -54.23) * mm});
            skPoint(sketch, "E3.18.4.1", {"position": v(126.75, -50.3) * mm});
            skPoint(sketch, "E3.18.5.0", {"position": v(119.89, -46.35) * mm});
            skPoint(sketch, "E3.18.5.1", {"position": v(126.75, -42.42) * mm});
            skPoint(sketch, "E3.18.6.0", {"position": v(119.89, -38.48) * mm});
            skPoint(sketch, "E3.18.6.1", {"position": v(126.75, -34.54) * mm});
            skPoint(sketch, "E3.18.7.0", {"position": v(119.89, -30.6) * mm});
            skPoint(sketch, "E3.18.7.1", {"position": v(126.75, -26.67) * mm});
            skPoint(sketch, "E3.18.8.0", {"position": v(119.89, -22.73) * mm});
            skPoint(sketch, "E3.18.8.1", {"position": v(126.75, -18.8) * mm});
            skPoint(sketch, "E3.18.9.0", {"position": v(119.89, -14.86) * mm});
            skPoint(sketch, "E3.18.9.1", {"position": v(126.75, -10.92) * mm});
            skPoint(sketch, "E3.18.10.0", {"position": v(119.89, -6.98) * mm});
            skPoint(sketch, "E3.18.10.1", {"position": v(126.75, -3.05) * mm});
            skPoint(sketch, "E3.18.11.0", {"position": v(119.89, 0.89) * mm});
            skPoint(sketch, "E3.18.11.1", {"position": v(126.75, 4.83) * mm});
            skPoint(sketch, "E3.18.12.0", {"position": v(119.89, 8.76) * mm});
            skPoint(sketch, "E3.18.12.1", {"position": v(126.75, 12.7) * mm});
            skPoint(sketch, "E3.18.13.0", {"position": v(119.89, 16.64) * mm});
            skPoint(sketch, "E3.18.13.1", {"position": v(126.75, 20.57) * mm});
            skPoint(sketch, "E3.18.14.0", {"position": v(119.89, 24.51) * mm});
            skPoint(sketch, "E3.18.14.1", {"position": v(126.75, 28.45) * mm});
            skPoint(sketch, "E3.18.15.0", {"position": v(119.89, 32.39) * mm});
            skPoint(sketch, "E3.18.15.1", {"position": v(126.75, 36.32) * mm});
            skPoint(sketch, "E3.18.16.0", {"position": v(119.89, 40.26) * mm});
            skPoint(sketch, "E3.18.16.1", {"position": v(126.75, 44.2) * mm});
            skPoint(sketch, "E3.18.17.0", {"position": v(119.89, 48.13) * mm});
            skPoint(sketch, "E3.18.17.1", {"position": v(126.75, 52.07) * mm});
            skPoint(sketch, "E3.19.0.0", {"position": v(133.6, -85.73) * mm});
            skPoint(sketch, "E3.19.0.1", {"position": v(140.46, -81.79) * mm});
            skPoint(sketch, "E3.19.1.0", {"position": v(133.6, -77.85) * mm});
            skPoint(sketch, "E3.19.1.1", {"position": v(140.46, -73.91) * mm});
            skPoint(sketch, "E3.19.2.0", {"position": v(133.6, -69.98) * mm});
            skPoint(sketch, "E3.19.2.1", {"position": v(140.46, -66.04) * mm});
            skPoint(sketch, "E3.19.3.0", {"position": v(133.6, -62.1) * mm});
            skPoint(sketch, "E3.19.3.1", {"position": v(140.46, -58.17) * mm});
            skPoint(sketch, "E3.19.4.0", {"position": v(133.6, -54.23) * mm});
            skPoint(sketch, "E3.19.4.1", {"position": v(140.46, -50.3) * mm});
            skPoint(sketch, "E3.19.5.0", {"position": v(133.6, -46.35) * mm});
            skPoint(sketch, "E3.19.5.1", {"position": v(140.46, -42.42) * mm});
            skPoint(sketch, "E3.19.6.0", {"position": v(133.6, -38.48) * mm});
            skPoint(sketch, "E3.19.6.1", {"position": v(140.46, -34.54) * mm});
            skPoint(sketch, "E3.19.7.0", {"position": v(133.6, -30.6) * mm});
            skPoint(sketch, "E3.19.7.1", {"position": v(140.46, -26.67) * mm});
            skPoint(sketch, "E3.19.8.0", {"position": v(133.6, -22.73) * mm});
            skPoint(sketch, "E3.19.8.1", {"position": v(140.46, -18.8) * mm});
            skPoint(sketch, "E3.19.9.0", {"position": v(133.6, -14.86) * mm});
            skPoint(sketch, "E3.19.9.1", {"position": v(140.46, -10.92) * mm});
            skPoint(sketch, "E3.19.10.0", {"position": v(133.6, -6.98) * mm});
            skPoint(sketch, "E3.19.10.1", {"position": v(140.46, -3.05) * mm});
            skPoint(sketch, "E3.19.11.0", {"position": v(133.6, 0.89) * mm});
            skPoint(sketch, "E3.19.11.1", {"position": v(140.46, 4.83) * mm});
            skPoint(sketch, "E3.19.12.0", {"position": v(133.6, 8.76) * mm});
            skPoint(sketch, "E3.19.12.1", {"position": v(140.46, 12.7) * mm});
            skPoint(sketch, "E3.19.13.0", {"position": v(133.6, 16.64) * mm});
            skPoint(sketch, "E3.19.13.1", {"position": v(140.46, 20.57) * mm});
            skPoint(sketch, "E3.19.14.0", {"position": v(133.6, 24.51) * mm});
            skPoint(sketch, "E3.19.14.1", {"position": v(140.46, 28.45) * mm});
            skPoint(sketch, "E3.19.15.0", {"position": v(133.6, 32.39) * mm});
            skPoint(sketch, "E3.19.15.1", {"position": v(140.46, 36.32) * mm});
            skPoint(sketch, "E3.19.16.0", {"position": v(133.6, 40.26) * mm});
            skPoint(sketch, "E3.19.16.1", {"position": v(140.46, 44.2) * mm});
            skPoint(sketch, "E3.19.17.0", {"position": v(133.6, 48.13) * mm});
            skPoint(sketch, "E3.19.17.1", {"position": v(140.46, 52.07) * mm});
            skPoint(sketch, "E3.20.0.0", {"position": v(147.32, -85.73) * mm});
            skPoint(sketch, "E3.20.0.1", {"position": v(154.18, -81.79) * mm});
            skPoint(sketch, "E3.20.1.0", {"position": v(147.32, -77.85) * mm});
            skPoint(sketch, "E3.20.1.1", {"position": v(154.18, -73.91) * mm});
            skPoint(sketch, "E3.20.2.0", {"position": v(147.32, -69.98) * mm});
            skPoint(sketch, "E3.20.2.1", {"position": v(154.18, -66.04) * mm});
            skPoint(sketch, "E3.20.3.0", {"position": v(147.32, -62.1) * mm});
            skPoint(sketch, "E3.20.3.1", {"position": v(154.18, -58.17) * mm});
            skPoint(sketch, "E3.20.4.0", {"position": v(147.32, -54.23) * mm});
            skPoint(sketch, "E3.20.4.1", {"position": v(154.18, -50.3) * mm});
            skPoint(sketch, "E3.20.5.0", {"position": v(147.32, -46.35) * mm});
            skPoint(sketch, "E3.20.5.1", {"position": v(154.18, -42.42) * mm});
            skPoint(sketch, "E3.20.6.0", {"position": v(147.32, -38.48) * mm});
            skPoint(sketch, "E3.20.6.1", {"position": v(154.18, -34.54) * mm});
            skPoint(sketch, "E3.20.7.0", {"position": v(147.32, -30.6) * mm});
            skPoint(sketch, "E3.20.7.1", {"position": v(154.18, -26.67) * mm});
            skPoint(sketch, "E3.20.8.0", {"position": v(147.32, -22.73) * mm});
            skPoint(sketch, "E3.20.8.1", {"position": v(154.18, -18.8) * mm});
            skPoint(sketch, "E3.20.9.0", {"position": v(147.32, -14.86) * mm});
            skPoint(sketch, "E3.20.9.1", {"position": v(154.18, -10.92) * mm});
            skPoint(sketch, "E3.20.10.0", {"position": v(147.32, -6.98) * mm});
            skPoint(sketch, "E3.20.10.1", {"position": v(154.18, -3.05) * mm});
            skPoint(sketch, "E3.20.11.0", {"position": v(147.32, 0.89) * mm});
            skPoint(sketch, "E3.20.11.1", {"position": v(154.18, 4.83) * mm});
            skPoint(sketch, "E3.20.12.0", {"position": v(147.32, 8.76) * mm});
            skPoint(sketch, "E3.20.12.1", {"position": v(154.18, 12.7) * mm});
            skPoint(sketch, "E3.20.13.0", {"position": v(147.32, 16.64) * mm});
            skPoint(sketch, "E3.20.13.1", {"position": v(154.18, 20.57) * mm});
            skPoint(sketch, "E3.20.14.0", {"position": v(147.32, 24.51) * mm});
            skPoint(sketch, "E3.20.14.1", {"position": v(154.18, 28.45) * mm});
            skPoint(sketch, "E3.20.15.0", {"position": v(147.32, 32.39) * mm});
            skPoint(sketch, "E3.20.15.1", {"position": v(154.18, 36.32) * mm});
            skPoint(sketch, "E3.20.16.0", {"position": v(147.32, 40.26) * mm});
            skPoint(sketch, "E3.20.16.1", {"position": v(154.18, 44.2) * mm});
            skPoint(sketch, "E3.20.17.0", {"position": v(147.32, 48.13) * mm});
            skPoint(sketch, "E3.20.17.1", {"position": v(154.18, 52.07) * mm});
            skPoint(sketch, "E3.21.0.0", {"position": v(161.04, -85.73) * mm});
            skPoint(sketch, "E3.21.0.1", {"position": v(167.9, -81.79) * mm});
            skPoint(sketch, "E3.21.1.0", {"position": v(161.04, -77.85) * mm});
            skPoint(sketch, "E3.21.1.1", {"position": v(167.9, -73.91) * mm});
            skPoint(sketch, "E3.21.2.0", {"position": v(161.04, -69.98) * mm});
            skPoint(sketch, "E3.21.2.1", {"position": v(167.9, -66.04) * mm});
            skPoint(sketch, "E3.21.3.0", {"position": v(161.04, -62.1) * mm});
            skPoint(sketch, "E3.21.3.1", {"position": v(167.9, -58.17) * mm});
            skPoint(sketch, "E3.21.4.0", {"position": v(161.04, -54.23) * mm});
            skPoint(sketch, "E3.21.4.1", {"position": v(167.9, -50.3) * mm});
            skPoint(sketch, "E3.21.5.0", {"position": v(161.04, -46.35) * mm});
            skPoint(sketch, "E3.21.5.1", {"position": v(167.9, -42.42) * mm});
            skPoint(sketch, "E3.21.6.0", {"position": v(161.04, -38.48) * mm});
            skPoint(sketch, "E3.21.6.1", {"position": v(167.9, -34.54) * mm});
            skPoint(sketch, "E3.21.7.0", {"position": v(161.04, -30.6) * mm});
            skPoint(sketch, "E3.21.7.1", {"position": v(167.9, -26.67) * mm});
            skPoint(sketch, "E3.21.8.0", {"position": v(161.04, -22.73) * mm});
            skPoint(sketch, "E3.21.8.1", {"position": v(167.9, -18.8) * mm});
            skPoint(sketch, "E3.21.9.0", {"position": v(161.04, -14.86) * mm});
            skPoint(sketch, "E3.21.9.1", {"position": v(167.9, -10.92) * mm});
            skPoint(sketch, "E3.21.10.0", {"position": v(161.04, -6.98) * mm});
            skPoint(sketch, "E3.21.10.1", {"position": v(167.9, -3.05) * mm});
            skPoint(sketch, "E3.21.11.0", {"position": v(161.04, 0.89) * mm});
            skPoint(sketch, "E3.21.11.1", {"position": v(167.9, 4.83) * mm});
            skPoint(sketch, "E3.21.12.0", {"position": v(161.04, 8.76) * mm});
            skPoint(sketch, "E3.21.12.1", {"position": v(167.9, 12.7) * mm});
            skPoint(sketch, "E3.21.13.0", {"position": v(161.04, 16.64) * mm});
            skPoint(sketch, "E3.21.13.1", {"position": v(167.9, 20.57) * mm});
            skPoint(sketch, "E3.21.14.0", {"position": v(161.04, 24.51) * mm});
            skPoint(sketch, "E3.21.14.1", {"position": v(167.9, 28.45) * mm});
            skPoint(sketch, "E3.21.15.0", {"position": v(161.04, 32.39) * mm});
            skPoint(sketch, "E3.21.15.1", {"position": v(167.9, 36.32) * mm});
            skPoint(sketch, "E3.21.16.0", {"position": v(161.04, 40.26) * mm});
            skPoint(sketch, "E3.21.16.1", {"position": v(167.9, 44.2) * mm});
            skPoint(sketch, "E3.21.17.0", {"position": v(161.04, 48.13) * mm});
            skPoint(sketch, "E3.21.17.1", {"position": v(167.9, 52.07) * mm});
            skPoint(sketch, "E3.22.0.0", {"position": v(174.75, -85.73) * mm});
            skPoint(sketch, "E3.22.0.1", {"position": v(181.61, -81.79) * mm});
            skPoint(sketch, "E3.22.1.0", {"position": v(174.75, -77.85) * mm});
            skPoint(sketch, "E3.22.1.1", {"position": v(181.61, -73.91) * mm});
            skPoint(sketch, "E3.22.2.0", {"position": v(174.75, -69.98) * mm});
            skPoint(sketch, "E3.22.2.1", {"position": v(181.61, -66.04) * mm});
            skPoint(sketch, "E3.22.3.0", {"position": v(174.75, -62.1) * mm});
            skPoint(sketch, "E3.22.3.1", {"position": v(181.61, -58.17) * mm});
            skPoint(sketch, "E3.22.4.0", {"position": v(174.75, -54.23) * mm});
            skPoint(sketch, "E3.22.4.1", {"position": v(181.61, -50.3) * mm});
            skPoint(sketch, "E3.22.5.0", {"position": v(174.75, -46.35) * mm});
            skPoint(sketch, "E3.22.5.1", {"position": v(181.61, -42.42) * mm});
            skPoint(sketch, "E3.22.6.0", {"position": v(174.75, -38.48) * mm});
            skPoint(sketch, "E3.22.6.1", {"position": v(181.61, -34.54) * mm});
            skPoint(sketch, "E3.22.7.0", {"position": v(174.75, -30.6) * mm});
            skPoint(sketch, "E3.22.7.1", {"position": v(181.61, -26.67) * mm});
            skPoint(sketch, "E3.22.8.0", {"position": v(174.75, -22.73) * mm});
            skPoint(sketch, "E3.22.8.1", {"position": v(181.61, -18.8) * mm});
            skPoint(sketch, "E3.22.9.0", {"position": v(174.75, -14.86) * mm});
            skPoint(sketch, "E3.22.9.1", {"position": v(181.61, -10.92) * mm});
            skPoint(sketch, "E3.22.10.0", {"position": v(174.75, -6.98) * mm});
            skPoint(sketch, "E3.22.10.1", {"position": v(181.61, -3.05) * mm});
            skPoint(sketch, "E3.22.11.0", {"position": v(174.75, 0.89) * mm});
            skPoint(sketch, "E3.22.11.1", {"position": v(181.61, 4.83) * mm});
            skPoint(sketch, "E3.22.12.0", {"position": v(174.75, 8.76) * mm});
            skPoint(sketch, "E3.22.12.1", {"position": v(181.61, 12.7) * mm});
            skPoint(sketch, "E3.22.13.0", {"position": v(174.75, 16.64) * mm});
            skPoint(sketch, "E3.22.13.1", {"position": v(181.61, 20.57) * mm});
            skPoint(sketch, "E3.22.14.0", {"position": v(174.75, 24.51) * mm});
            skPoint(sketch, "E3.22.14.1", {"position": v(181.61, 28.45) * mm});
            skPoint(sketch, "E3.22.15.0", {"position": v(174.75, 32.39) * mm});
            skPoint(sketch, "E3.22.15.1", {"position": v(181.61, 36.32) * mm});
            skPoint(sketch, "E3.22.16.0", {"position": v(174.75, 40.26) * mm});
            skPoint(sketch, "E3.22.16.1", {"position": v(181.61, 44.2) * mm});
            skPoint(sketch, "E3.22.17.0", {"position": v(174.75, 48.13) * mm});
            skPoint(sketch, "E3.22.17.1", {"position": v(181.61, 52.07) * mm});
            skLineSegment(sketch, "E3.direction1", {"start": v(-127, -85.73) * mm, "end": v(-113.28, -85.73) * mm, "construction": true});
            skLineSegment(sketch, "E3.direction2", {"start": v(-127, -85.73) * mm, "end": v(-127, -77.85) * mm, "construction": true});
            skSolve(sketch);
        }
        {
            var Q0;
            Q0=makeQuery(id+"F0.imprint","IMPRINT",FACE,{"disambiguationData":[TD([[makeQuery(id+"F0.imprint","IMPRINT",EDGE,{"derivedFrom":sQuery(id+"F0.wireOp",EDGE,"E0.bottom")}),-1.0]])]});
            extrude(context, id + "F1", {"entities" : qUnion([Q0]), "depth" : 1.59 * mm});
        }
        {
            var Q0;
            Q0=sQuery(id+"F0.wireOp",VERTEX,"E3.1.5.1");
            var Q1;
            Q1=sQuery(id+"F0.wireOp",VERTEX,"E3.0.16.1");
            var Q2;
            Q2=sQuery(id+"F0.wireOp",VERTEX,"E3.0.8.1");
            var Q3;
            Q3=sQuery(id+"F0.wireOp",VERTEX,"E3.1.13.1");
            var Q4;
            Q4=sQuery(id+"F0.wireOp",VERTEX,"E3.1.6.0");
            var Q5;
            Q5=sQuery(id+"F0.wireOp",VERTEX,"E3.0.17.0");
            var Q6;
            Q6=sQuery(id+"F0.wireOp",VERTEX,"E3.0.9.0");
            var Q7;
            Q7=sQuery(id+"F0.wireOp",VERTEX,"E3.2.11.0");
            var Q8;
            Q8=sQuery(id+"F0.wireOp",VERTEX,"E3.2.3.0");
            var Q9;
            Q9=sQuery(id+"F0.wireOp",VERTEX,"E3.1.14.0");
            var Q10;
            Q10=sQuery(id+"F0.wireOp",VERTEX,"E3.1.6.1");
            var Q11;
            Q11=sQuery(id+"F0.wireOp",VERTEX,"E3.0.17.1");
            var Q12;
            Q12=sQuery(id+"F0.wireOp",VERTEX,"E3.0.9.1");
            var Q13;
            Q13=sQuery(id+"F0.wireOp",VERTEX,"E3.1.14.1");
            var Q14;
            Q14=sQuery(id+"F0.wireOp",VERTEX,"E3.1.7.0");
            var Q15;
            Q15=sQuery(id+"F0.wireOp",VERTEX,"E3.0.18.0");
            var Q16;
            Q16=sQuery(id+"F0.wireOp",VERTEX,"E3.0.10.0");
            var Q17;
            Q17=sQuery(id+"F0.wireOp",VERTEX,"E3.0.2.0");
            var Q18;
            Q18=sQuery(id+"F0.wireOp",VERTEX,"E3.2.12.0");
            var Q19;
            Q19=sQuery(id+"F0.wireOp",VERTEX,"E3.2.4.0");
            var Q20;
            Q20=sQuery(id+"F0.wireOp",VERTEX,"E3.1.15.0");
            var Q21;
            Q21=sQuery(id+"F0.wireOp",VERTEX,"E3.1.7.1");
            var Q22;
            Q22=sQuery(id+"F0.wireOp",VERTEX,"E3.0.18.1");
            var Q23;
            Q23=sQuery(id+"F0.wireOp",VERTEX,"E3.0.10.1");
            var Q24;
            Q24=sQuery(id+"F0.wireOp",VERTEX,"E3.0.2.1");
            var Q25;
            Q25=sQuery(id+"F0.wireOp",VERTEX,"E3.1.15.1");
            var Q26;
            Q26=sQuery(id+"F0.wireOp",VERTEX,"E3.1.8.0");
            var Q27;
            Q27=sQuery(id+"F0.wireOp",VERTEX,"E3.1.0.0");
            var Q28;
            Q28=sQuery(id+"F0.wireOp",VERTEX,"E3.0.11.0");
            var Q29;
            Q29=sQuery(id+"F0.wireOp",VERTEX,"E3.0.3.0");
            var Q30;
            Q30=sQuery(id+"F0.wireOp",VERTEX,"E3.2.13.0");
            var Q31;
            Q31=sQuery(id+"F0.wireOp",VERTEX,"E3.2.5.0");
            var Q32;
            Q32=sQuery(id+"F0.wireOp",VERTEX,"E3.1.16.0");
            var Q33;
            Q33=sQuery(id+"F0.wireOp",VERTEX,"E3.1.8.1");
            var Q34;
            Q34=sQuery(id+"F0.wireOp",VERTEX,"E3.1.0.1");
            var Q35;
            Q35=sQuery(id+"F0.wireOp",VERTEX,"E3.0.11.1");
            var Q36;
            Q36=sQuery(id+"F0.wireOp",VERTEX,"E3.0.3.1");
            var Q37;
            Q37=sQuery(id+"F0.wireOp",VERTEX,"E3.1.16.1");
            var Q38;
            Q38=sQuery(id+"F0.wireOp",VERTEX,"E3.1.9.0");
            var Q39;
            Q39=sQuery(id+"F0.wireOp",VERTEX,"E3.1.1.0");
            var Q40;
            Q40=sQuery(id+"F0.wireOp",VERTEX,"E3.0.12.0");
            var Q41;
            Q41=sQuery(id+"F0.wireOp",VERTEX,"E3.0.4.0");
            var Q42;
            Q42=sQuery(id+"F0.wireOp",VERTEX,"E3.2.14.0");
            var Q43;
            Q43=sQuery(id+"F0.wireOp",VERTEX,"E3.2.6.0");
            var Q44;
            Q44=sQuery(id+"F0.wireOp",VERTEX,"E3.1.17.0");
            var Q45;
            Q45=sQuery(id+"F0.wireOp",VERTEX,"E3.1.9.1");
            var Q46;
            Q46=sQuery(id+"F0.wireOp",VERTEX,"E3.1.1.1");
            var Q47;
            Q47=sQuery(id+"F0.wireOp",VERTEX,"E3.0.12.1");
            var Q48;
            Q48=sQuery(id+"F0.wireOp",VERTEX,"E3.0.4.1");
            var Q49;
            Q49=sQuery(id+"F0.wireOp",VERTEX,"E3.1.17.1");
            var Q50;
            Q50=sQuery(id+"F0.wireOp",VERTEX,"E3.1.10.0");
            var Q51;
            Q51=sQuery(id+"F0.wireOp",VERTEX,"E3.1.2.0");
            var Q52;
            Q52=sQuery(id+"F0.wireOp",VERTEX,"E3.0.13.0");
            var Q53;
            Q53=sQuery(id+"F0.wireOp",VERTEX,"E3.0.5.0");
            var Q54;
            Q54=sQuery(id+"F0.wireOp",VERTEX,"E3.2.15.0");
            var Q55;
            Q55=sQuery(id+"F0.wireOp",VERTEX,"E3.2.7.0");
            var Q56;
            Q56=sQuery(id+"F0.wireOp",VERTEX,"E3.1.18.0");
            var Q57;
            Q57=sQuery(id+"F0.wireOp",VERTEX,"E3.0.13.1");
            var Q58;
            Q58=sQuery(id+"F0.wireOp",VERTEX,"E3.0.5.1");
            var Q59;
            Q59=sQuery(id+"F0.wireOp",VERTEX,"E3.1.18.1");
            var Q60;
            Q60=sQuery(id+"F0.wireOp",VERTEX,"E3.1.10.1");
            var Q61;
            Q61=sQuery(id+"F0.wireOp",VERTEX,"E3.1.2.1");
            var Q62;
            Q62=sQuery(id+"F0.wireOp",VERTEX,"E3.0.14.0");
            var Q63;
            Q63=sQuery(id+"F0.wireOp",VERTEX,"E3.0.6.0");
            var Q64;
            Q64=sQuery(id+"F0.wireOp",VERTEX,"E3.2.8.0");
            var Q65;
            Q65=sQuery(id+"F0.wireOp",VERTEX,"E3.2.0.0");
            var Q66;
            Q66=sQuery(id+"F0.wireOp",VERTEX,"E3.1.11.0");
            var Q67;
            Q67=sQuery(id+"F0.wireOp",VERTEX,"E3.1.3.0");
            var Q68;
            Q68=sQuery(id+"F0.wireOp",VERTEX,"E3.2.16.0");
            var Q69;
            Q69=sQuery(id+"F0.wireOp",VERTEX,"E3.0.14.1");
            var Q70;
            Q70=sQuery(id+"F0.wireOp",VERTEX,"E3.0.6.1");
            var Q71;
            Q71=sQuery(id+"F0.wireOp",VERTEX,"E3.1.11.1");
            var Q72;
            Q72=sQuery(id+"F0.wireOp",VERTEX,"E3.1.3.1");
            var Q73;
            Q73=sQuery(id+"F0.wireOp",VERTEX,"E3.0.15.0");
            var Q74;
            Q74=sQuery(id+"F0.wireOp",VERTEX,"E3.0.7.0");
            var Q75;
            Q75=sQuery(id+"F0.wireOp",VERTEX,"E3.2.9.0");
            var Q76;
            Q76=sQuery(id+"F0.wireOp",VERTEX,"E3.2.1.0");
            var Q77;
            Q77=sQuery(id+"F0.wireOp",VERTEX,"E3.1.12.0");
            var Q78;
            Q78=sQuery(id+"F0.wireOp",VERTEX,"E3.1.4.0");
            var Q79;
            Q79=sQuery(id+"F0.wireOp",VERTEX,"E3.2.17.0");
            var Q80;
            Q80=sQuery(id+"F0.wireOp",VERTEX,"E3.0.15.1");
            var Q81;
            Q81=sQuery(id+"F0.wireOp",VERTEX,"E3.0.7.1");
            var Q82;
            Q82=sQuery(id+"F0.wireOp",VERTEX,"E3.1.12.1");
            var Q83;
            Q83=sQuery(id+"F0.wireOp",VERTEX,"E3.1.4.1");
            var Q84;
            Q84=sQuery(id+"F0.wireOp",VERTEX,"E3.0.16.0");
            var Q85;
            Q85=sQuery(id+"F0.wireOp",VERTEX,"E3.0.8.0");
            var Q86;
            Q86=sQuery(id+"F0.wireOp",VERTEX,"E3.2.10.0");
            var Q87;
            Q87=sQuery(id+"F0.wireOp",VERTEX,"E3.2.2.0");
            var Q88;
            Q88=sQuery(id+"F0.wireOp",VERTEX,"E3.1.13.0");
            var Q89;
            Q89=sQuery(id+"F0.wireOp",VERTEX,"E3.1.5.0");
            var Q90;
            Q90=sQuery(id+"F0.wireOp",VERTEX,"E3.2.18.0");
            var Q91;
            Q91=sQuery(id+"F0.wireOp",VERTEX,"E2");
            var Q92;
            Q92=sQuery(id+"F0.wireOp",VERTEX,"E3.0.1.0");
            var Q93;
            Q93=sQuery(id+"F0.wireOp",VERTEX,"E3.0.1.1");
            var Q94;
            Q94=makeQuery(id+"F1.opExtrude","SWEPT_BODY",BODY,{"disambiguationData":[OSD([sQuery(id+"F0.wireOp",EDGE,"E0.bottom"),sQuery(id+"F0.wireOp",EDGE,"E0.top"),sQuery(id+"F0.wireOp",EDGE,"E0.left"),sQuery(id+"F0.wireOp",EDGE,"E0.right")])]});
            hole(context, id + "F2", {"style" : HoleStyle.SIMPLE, "endStyle" : HoleEndStyle.THROUGH, "oppositeDirection" : true, "holeDiameter" : 6.35 * mm, "tappedDepth" : 12.7 * mm, "tapClearance" : 3, "startFromSketch" : true, "locations" : qUnion([Q0, Q1, Q2, Q3, Q4, Q5, Q6, Q7, Q8, Q9, Q10, Q11, Q12, Q13, Q14, Q15, Q16, Q17, Q18, Q19, Q20, Q21, Q22, Q23, Q24, Q25, Q26, Q27, Q28, Q29, Q30, Q31, Q32, Q33, Q34, Q35, Q36, Q37, Q38, Q39, Q40, Q41, Q42, Q43, Q44, Q45, Q46, Q47, Q48, Q49, Q50, Q51, Q52, Q53, Q54, Q55, Q56, Q57, Q58, Q59, Q60, Q61, Q62, Q63, Q64, Q65, Q66, Q67, Q68, Q69, Q70, Q71, Q72, Q73, Q74, Q75, Q76, Q77, Q78, Q79, Q80, Q81, Q82, Q83, Q84, Q85, Q86, Q87, Q88, Q89, Q90, Q91, Q92, Q93]), "scope" : qUnion([Q94])});
        }
        {
            var Q0;
            Q0=sQuery(id+"F0.wireOp",VERTEX,"E3.2.2.1");
            var Q1;
            Q1=sQuery(id+"F0.wireOp",VERTEX,"E3.3.7.1");
            var Q2;
            Q2=sQuery(id+"F0.wireOp",VERTEX,"E3.4.4.1");
            var Q3;
            Q3=sQuery(id+"F0.wireOp",VERTEX,"E3.3.15.1");
            var Q4;
            Q4=sQuery(id+"F0.wireOp",VERTEX,"E3.2.18.1");
            var Q5;
            Q5=sQuery(id+"F0.wireOp",VERTEX,"E3.4.12.1");
            var Q6;
            Q6=sQuery(id+"F0.wireOp",VERTEX,"E3.2.10.1");
            var Q7;
            Q7=sQuery(id+"F0.wireOp",VERTEX,"E3.3.0.0");
            var Q8;
            Q8=sQuery(id+"F0.wireOp",VERTEX,"E3.4.13.0");
            var Q9;
            Q9=sQuery(id+"F0.wireOp",VERTEX,"E3.4.5.0");
            var Q10;
            Q10=sQuery(id+"F0.wireOp",VERTEX,"E3.3.16.0");
            var Q11;
            Q11=sQuery(id+"F0.wireOp",VERTEX,"E3.3.8.0");
            var Q12;
            Q12=sQuery(id+"F0.wireOp",VERTEX,"E3.3.0.1");
            var Q13;
            Q13=sQuery(id+"F0.wireOp",VERTEX,"E3.2.11.1");
            var Q14;
            Q14=sQuery(id+"F0.wireOp",VERTEX,"E3.2.3.1");
            var Q15;
            Q15=sQuery(id+"F0.wireOp",VERTEX,"E3.4.13.1");
            var Q16;
            Q16=sQuery(id+"F0.wireOp",VERTEX,"E3.4.5.1");
            var Q17;
            Q17=sQuery(id+"F0.wireOp",VERTEX,"E3.3.16.1");
            var Q18;
            Q18=sQuery(id+"F0.wireOp",VERTEX,"E3.3.8.1");
            var Q19;
            Q19=sQuery(id+"F0.wireOp",VERTEX,"E3.3.1.0");
            var Q20;
            Q20=sQuery(id+"F0.wireOp",VERTEX,"E3.4.14.0");
            var Q21;
            Q21=sQuery(id+"F0.wireOp",VERTEX,"E3.4.6.0");
            var Q22;
            Q22=sQuery(id+"F0.wireOp",VERTEX,"E3.3.17.0");
            var Q23;
            Q23=sQuery(id+"F0.wireOp",VERTEX,"E3.3.9.0");
            var Q24;
            Q24=sQuery(id+"F0.wireOp",VERTEX,"E3.3.1.1");
            var Q25;
            Q25=sQuery(id+"F0.wireOp",VERTEX,"E3.2.12.1");
            var Q26;
            Q26=sQuery(id+"F0.wireOp",VERTEX,"E3.2.4.1");
            var Q27;
            Q27=sQuery(id+"F0.wireOp",VERTEX,"E3.4.14.1");
            var Q28;
            Q28=sQuery(id+"F0.wireOp",VERTEX,"E3.4.6.1");
            var Q29;
            Q29=sQuery(id+"F0.wireOp",VERTEX,"E3.3.17.1");
            var Q30;
            Q30=sQuery(id+"F0.wireOp",VERTEX,"E3.3.9.1");
            var Q31;
            Q31=sQuery(id+"F0.wireOp",VERTEX,"E3.3.2.0");
            var Q32;
            Q32=sQuery(id+"F0.wireOp",VERTEX,"E3.4.15.0");
            var Q33;
            Q33=sQuery(id+"F0.wireOp",VERTEX,"E3.4.7.0");
            var Q34;
            Q34=sQuery(id+"F0.wireOp",VERTEX,"E3.3.18.0");
            var Q35;
            Q35=sQuery(id+"F0.wireOp",VERTEX,"E3.3.10.0");
            var Q36;
            Q36=sQuery(id+"F0.wireOp",VERTEX,"E3.3.2.1");
            var Q37;
            Q37=sQuery(id+"F0.wireOp",VERTEX,"E3.2.13.1");
            var Q38;
            Q38=sQuery(id+"F0.wireOp",VERTEX,"E3.2.5.1");
            var Q39;
            Q39=sQuery(id+"F0.wireOp",VERTEX,"E3.4.15.1");
            var Q40;
            Q40=sQuery(id+"F0.wireOp",VERTEX,"E3.4.7.1");
            var Q41;
            Q41=sQuery(id+"F0.wireOp",VERTEX,"E3.3.18.1");
            var Q42;
            Q42=sQuery(id+"F0.wireOp",VERTEX,"E3.3.10.1");
            var Q43;
            Q43=sQuery(id+"F0.wireOp",VERTEX,"E3.3.3.0");
            var Q44;
            Q44=sQuery(id+"F0.wireOp",VERTEX,"E3.4.16.0");
            var Q45;
            Q45=sQuery(id+"F0.wireOp",VERTEX,"E3.4.8.0");
            var Q46;
            Q46=sQuery(id+"F0.wireOp",VERTEX,"E3.4.0.0");
            var Q47;
            Q47=sQuery(id+"F0.wireOp",VERTEX,"E3.3.11.0");
            var Q48;
            Q48=sQuery(id+"F0.wireOp",VERTEX,"E3.3.3.1");
            var Q49;
            Q49=sQuery(id+"F0.wireOp",VERTEX,"E3.2.14.1");
            var Q50;
            Q50=sQuery(id+"F0.wireOp",VERTEX,"E3.2.6.1");
            var Q51;
            Q51=sQuery(id+"F0.wireOp",VERTEX,"E3.4.16.1");
            var Q52;
            Q52=sQuery(id+"F0.wireOp",VERTEX,"E3.4.8.1");
            var Q53;
            Q53=sQuery(id+"F0.wireOp",VERTEX,"E3.4.0.1");
            var Q54;
            Q54=sQuery(id+"F0.wireOp",VERTEX,"E3.3.11.1");
            var Q55;
            Q55=sQuery(id+"F0.wireOp",VERTEX,"E3.3.4.0");
            var Q56;
            Q56=sQuery(id+"F0.wireOp",VERTEX,"E3.4.17.0");
            var Q57;
            Q57=sQuery(id+"F0.wireOp",VERTEX,"E3.4.9.0");
            var Q58;
            Q58=sQuery(id+"F0.wireOp",VERTEX,"E3.4.1.0");
            var Q59;
            Q59=sQuery(id+"F0.wireOp",VERTEX,"E3.3.12.0");
            var Q60;
            Q60=sQuery(id+"F0.wireOp",VERTEX,"E3.4.1.1");
            var Q61;
            Q61=sQuery(id+"F0.wireOp",VERTEX,"E3.3.12.1");
            var Q62;
            Q62=sQuery(id+"F0.wireOp",VERTEX,"E3.3.4.1");
            var Q63;
            Q63=sQuery(id+"F0.wireOp",VERTEX,"E3.2.15.1");
            var Q64;
            Q64=sQuery(id+"F0.wireOp",VERTEX,"E3.4.17.1");
            var Q65;
            Q65=sQuery(id+"F0.wireOp",VERTEX,"E3.4.9.1");
            var Q66;
            Q66=sQuery(id+"F0.wireOp",VERTEX,"E3.2.7.1");
            var Q67;
            Q67=sQuery(id+"F0.wireOp",VERTEX,"E3.4.18.0");
            var Q68;
            Q68=sQuery(id+"F0.wireOp",VERTEX,"E3.4.10.0");
            var Q69;
            Q69=sQuery(id+"F0.wireOp",VERTEX,"E3.4.2.0");
            var Q70;
            Q70=sQuery(id+"F0.wireOp",VERTEX,"E3.3.13.0");
            var Q71;
            Q71=sQuery(id+"F0.wireOp",VERTEX,"E3.3.5.0");
            var Q72;
            Q72=sQuery(id+"F0.wireOp",VERTEX,"E3.2.8.1");
            var Q73;
            Q73=sQuery(id+"F0.wireOp",VERTEX,"E3.2.0.1");
            var Q74;
            Q74=sQuery(id+"F0.wireOp",VERTEX,"E3.4.2.1");
            var Q75;
            Q75=sQuery(id+"F0.wireOp",VERTEX,"E3.3.13.1");
            var Q76;
            Q76=sQuery(id+"F0.wireOp",VERTEX,"E3.3.5.1");
            var Q77;
            Q77=sQuery(id+"F0.wireOp",VERTEX,"E3.2.16.1");
            var Q78;
            Q78=sQuery(id+"F0.wireOp",VERTEX,"E3.4.18.1");
            var Q79;
            Q79=sQuery(id+"F0.wireOp",VERTEX,"E3.4.10.1");
            var Q80;
            Q80=sQuery(id+"F0.wireOp",VERTEX,"E3.4.3.0");
            var Q81;
            Q81=sQuery(id+"F0.wireOp",VERTEX,"E3.3.14.0");
            var Q82;
            Q82=sQuery(id+"F0.wireOp",VERTEX,"E3.3.6.0");
            var Q83;
            Q83=sQuery(id+"F0.wireOp",VERTEX,"E3.4.11.0");
            var Q84;
            Q84=sQuery(id+"F0.wireOp",VERTEX,"E3.2.9.1");
            var Q85;
            Q85=sQuery(id+"F0.wireOp",VERTEX,"E3.2.1.1");
            var Q86;
            Q86=sQuery(id+"F0.wireOp",VERTEX,"E3.4.3.1");
            var Q87;
            Q87=sQuery(id+"F0.wireOp",VERTEX,"E3.3.14.1");
            var Q88;
            Q88=sQuery(id+"F0.wireOp",VERTEX,"E3.3.6.1");
            var Q89;
            Q89=sQuery(id+"F0.wireOp",VERTEX,"E3.2.17.1");
            var Q90;
            Q90=sQuery(id+"F0.wireOp",VERTEX,"E3.4.11.1");
            var Q91;
            Q91=sQuery(id+"F0.wireOp",VERTEX,"E3.4.4.0");
            var Q92;
            Q92=sQuery(id+"F0.wireOp",VERTEX,"E3.3.15.0");
            var Q93;
            Q93=sQuery(id+"F0.wireOp",VERTEX,"E3.3.7.0");
            var Q94;
            Q94=sQuery(id+"F0.wireOp",VERTEX,"E3.4.12.0");
            var Q95;
            Q95=makeQuery(id+"F1.opExtrude","SWEPT_BODY",BODY,{"disambiguationData":[OSD([sQuery(id+"F0.wireOp",EDGE,"E0.bottom"),sQuery(id+"F0.wireOp",EDGE,"E0.top"),sQuery(id+"F0.wireOp",EDGE,"E0.left"),sQuery(id+"F0.wireOp",EDGE,"E0.right")])]});
            hole(context, id + "F3", {"style" : HoleStyle.SIMPLE, "endStyle" : HoleEndStyle.THROUGH, "oppositeDirection" : true, "holeDiameter" : 6.35 * mm, "tappedDepth" : 12.7 * mm, "tapClearance" : 3, "startFromSketch" : true, "locations" : qUnion([Q0, Q1, Q2, Q3, Q4, Q5, Q6, Q7, Q8, Q9, Q10, Q11, Q12, Q13, Q14, Q15, Q16, Q17, Q18, Q19, Q20, Q21, Q22, Q23, Q24, Q25, Q26, Q27, Q28, Q29, Q30, Q31, Q32, Q33, Q34, Q35, Q36, Q37, Q38, Q39, Q40, Q41, Q42, Q43, Q44, Q45, Q46, Q47, Q48, Q49, Q50, Q51, Q52, Q53, Q54, Q55, Q56, Q57, Q58, Q59, Q60, Q61, Q62, Q63, Q64, Q65, Q66, Q67, Q68, Q69, Q70, Q71, Q72, Q73, Q74, Q75, Q76, Q77, Q78, Q79, Q80, Q81, Q82, Q83, Q84, Q85, Q86, Q87, Q88, Q89, Q90, Q91, Q92, Q93, Q94]), "scope" : qUnion([Q95])});
        }
        {
            var Q0;
            Q0=sQuery(id+"F0.wireOp",VERTEX,"E3.6.14.1");
            var Q1;
            Q1=sQuery(id+"F0.wireOp",VERTEX,"E3.5.1.1");
            var Q2;
            Q2=sQuery(id+"F0.wireOp",VERTEX,"E3.5.9.1");
            var Q3;
            Q3=sQuery(id+"F0.wireOp",VERTEX,"E3.6.6.1");
            var Q4;
            Q4=sQuery(id+"F0.wireOp",VERTEX,"E3.5.17.1");
            var Q5;
            Q5=sQuery(id+"F0.wireOp",VERTEX,"E3.6.7.0");
            var Q6;
            Q6=sQuery(id+"F0.wireOp",VERTEX,"E3.5.18.0");
            var Q7;
            Q7=sQuery(id+"F0.wireOp",VERTEX,"E3.5.10.0");
            var Q8;
            Q8=sQuery(id+"F0.wireOp",VERTEX,"E3.5.2.0");
            var Q9;
            Q9=sQuery(id+"F0.wireOp",VERTEX,"E3.7.12.0");
            var Q10;
            Q10=sQuery(id+"F0.wireOp",VERTEX,"E3.7.4.0");
            var Q11;
            Q11=sQuery(id+"F0.wireOp",VERTEX,"E3.6.15.0");
            var Q12;
            Q12=sQuery(id+"F0.wireOp",VERTEX,"E3.6.7.1");
            var Q13;
            Q13=sQuery(id+"F0.wireOp",VERTEX,"E3.5.18.1");
            var Q14;
            Q14=sQuery(id+"F0.wireOp",VERTEX,"E3.5.10.1");
            var Q15;
            Q15=sQuery(id+"F0.wireOp",VERTEX,"E3.5.2.1");
            var Q16;
            Q16=sQuery(id+"F0.wireOp",VERTEX,"E3.6.15.1");
            var Q17;
            Q17=sQuery(id+"F0.wireOp",VERTEX,"E3.6.8.0");
            var Q18;
            Q18=sQuery(id+"F0.wireOp",VERTEX,"E3.6.0.0");
            var Q19;
            Q19=sQuery(id+"F0.wireOp",VERTEX,"E3.5.11.0");
            var Q20;
            Q20=sQuery(id+"F0.wireOp",VERTEX,"E3.5.3.0");
            var Q21;
            Q21=sQuery(id+"F0.wireOp",VERTEX,"E3.7.13.0");
            var Q22;
            Q22=sQuery(id+"F0.wireOp",VERTEX,"E3.7.5.0");
            var Q23;
            Q23=sQuery(id+"F0.wireOp",VERTEX,"E3.6.16.0");
            var Q24;
            Q24=sQuery(id+"F0.wireOp",VERTEX,"E3.6.8.1");
            var Q25;
            Q25=sQuery(id+"F0.wireOp",VERTEX,"E3.6.0.1");
            var Q26;
            Q26=sQuery(id+"F0.wireOp",VERTEX,"E3.5.11.1");
            var Q27;
            Q27=sQuery(id+"F0.wireOp",VERTEX,"E3.5.3.1");
            var Q28;
            Q28=sQuery(id+"F0.wireOp",VERTEX,"E3.6.16.1");
            var Q29;
            Q29=sQuery(id+"F0.wireOp",VERTEX,"E3.6.9.0");
            var Q30;
            Q30=sQuery(id+"F0.wireOp",VERTEX,"E3.6.1.0");
            var Q31;
            Q31=sQuery(id+"F0.wireOp",VERTEX,"E3.5.12.0");
            var Q32;
            Q32=sQuery(id+"F0.wireOp",VERTEX,"E3.5.4.0");
            var Q33;
            Q33=sQuery(id+"F0.wireOp",VERTEX,"E3.7.14.0");
            var Q34;
            Q34=sQuery(id+"F0.wireOp",VERTEX,"E3.7.6.0");
            var Q35;
            Q35=sQuery(id+"F0.wireOp",VERTEX,"E3.6.17.0");
            var Q36;
            Q36=sQuery(id+"F0.wireOp",VERTEX,"E3.6.9.1");
            var Q37;
            Q37=sQuery(id+"F0.wireOp",VERTEX,"E3.6.1.1");
            var Q38;
            Q38=sQuery(id+"F0.wireOp",VERTEX,"E3.5.12.1");
            var Q39;
            Q39=sQuery(id+"F0.wireOp",VERTEX,"E3.5.4.1");
            var Q40;
            Q40=sQuery(id+"F0.wireOp",VERTEX,"E3.6.17.1");
            var Q41;
            Q41=sQuery(id+"F0.wireOp",VERTEX,"E3.6.10.0");
            var Q42;
            Q42=sQuery(id+"F0.wireOp",VERTEX,"E3.6.2.0");
            var Q43;
            Q43=sQuery(id+"F0.wireOp",VERTEX,"E3.5.13.0");
            var Q44;
            Q44=sQuery(id+"F0.wireOp",VERTEX,"E3.5.5.0");
            var Q45;
            Q45=sQuery(id+"F0.wireOp",VERTEX,"E3.7.15.0");
            var Q46;
            Q46=sQuery(id+"F0.wireOp",VERTEX,"E3.7.7.0");
            var Q47;
            Q47=sQuery(id+"F0.wireOp",VERTEX,"E3.6.18.0");
            var Q48;
            Q48=sQuery(id+"F0.wireOp",VERTEX,"E3.6.10.1");
            var Q49;
            Q49=sQuery(id+"F0.wireOp",VERTEX,"E3.6.2.1");
            var Q50;
            Q50=sQuery(id+"F0.wireOp",VERTEX,"E3.5.13.1");
            var Q51;
            Q51=sQuery(id+"F0.wireOp",VERTEX,"E3.5.5.1");
            var Q52;
            Q52=sQuery(id+"F0.wireOp",VERTEX,"E3.6.18.1");
            var Q53;
            Q53=sQuery(id+"F0.wireOp",VERTEX,"E3.6.11.0");
            var Q54;
            Q54=sQuery(id+"F0.wireOp",VERTEX,"E3.6.3.0");
            var Q55;
            Q55=sQuery(id+"F0.wireOp",VERTEX,"E3.5.14.0");
            var Q56;
            Q56=sQuery(id+"F0.wireOp",VERTEX,"E3.5.6.0");
            var Q57;
            Q57=sQuery(id+"F0.wireOp",VERTEX,"E3.7.16.0");
            var Q58;
            Q58=sQuery(id+"F0.wireOp",VERTEX,"E3.7.8.0");
            var Q59;
            Q59=sQuery(id+"F0.wireOp",VERTEX,"E3.7.0.0");
            var Q60;
            Q60=sQuery(id+"F0.wireOp",VERTEX,"E3.5.14.1");
            var Q61;
            Q61=sQuery(id+"F0.wireOp",VERTEX,"E3.5.6.1");
            var Q62;
            Q62=sQuery(id+"F0.wireOp",VERTEX,"E3.6.11.1");
            var Q63;
            Q63=sQuery(id+"F0.wireOp",VERTEX,"E3.6.3.1");
            var Q64;
            Q64=sQuery(id+"F0.wireOp",VERTEX,"E3.5.15.0");
            var Q65;
            Q65=sQuery(id+"F0.wireOp",VERTEX,"E3.5.7.0");
            var Q66;
            Q66=sQuery(id+"F0.wireOp",VERTEX,"E3.7.9.0");
            var Q67;
            Q67=sQuery(id+"F0.wireOp",VERTEX,"E3.7.1.0");
            var Q68;
            Q68=sQuery(id+"F0.wireOp",VERTEX,"E3.6.12.0");
            var Q69;
            Q69=sQuery(id+"F0.wireOp",VERTEX,"E3.6.4.0");
            var Q70;
            Q70=sQuery(id+"F0.wireOp",VERTEX,"E3.7.17.0");
            var Q71;
            Q71=sQuery(id+"F0.wireOp",VERTEX,"E3.6.12.1");
            var Q72;
            Q72=sQuery(id+"F0.wireOp",VERTEX,"E3.6.4.1");
            var Q73;
            Q73=sQuery(id+"F0.wireOp",VERTEX,"E3.5.15.1");
            var Q74;
            Q74=sQuery(id+"F0.wireOp",VERTEX,"E3.5.7.1");
            var Q75;
            Q75=sQuery(id+"F0.wireOp",VERTEX,"E3.7.18.0");
            var Q76;
            Q76=sQuery(id+"F0.wireOp",VERTEX,"E3.5.16.0");
            var Q77;
            Q77=sQuery(id+"F0.wireOp",VERTEX,"E3.5.8.0");
            var Q78;
            Q78=sQuery(id+"F0.wireOp",VERTEX,"E3.5.0.0");
            var Q79;
            Q79=sQuery(id+"F0.wireOp",VERTEX,"E3.7.10.0");
            var Q80;
            Q80=sQuery(id+"F0.wireOp",VERTEX,"E3.7.2.0");
            var Q81;
            Q81=sQuery(id+"F0.wireOp",VERTEX,"E3.6.13.0");
            var Q82;
            Q82=sQuery(id+"F0.wireOp",VERTEX,"E3.6.5.0");
            var Q83;
            Q83=sQuery(id+"F0.wireOp",VERTEX,"E3.5.16.1");
            var Q84;
            Q84=sQuery(id+"F0.wireOp",VERTEX,"E3.5.8.1");
            var Q85;
            Q85=sQuery(id+"F0.wireOp",VERTEX,"E3.5.0.1");
            var Q86;
            Q86=sQuery(id+"F0.wireOp",VERTEX,"E3.6.13.1");
            var Q87;
            Q87=sQuery(id+"F0.wireOp",VERTEX,"E3.6.5.1");
            var Q88;
            Q88=sQuery(id+"F0.wireOp",VERTEX,"E3.5.17.0");
            var Q89;
            Q89=sQuery(id+"F0.wireOp",VERTEX,"E3.5.9.0");
            var Q90;
            Q90=sQuery(id+"F0.wireOp",VERTEX,"E3.5.1.0");
            var Q91;
            Q91=sQuery(id+"F0.wireOp",VERTEX,"E3.7.11.0");
            var Q92;
            Q92=sQuery(id+"F0.wireOp",VERTEX,"E3.7.3.0");
            var Q93;
            Q93=sQuery(id+"F0.wireOp",VERTEX,"E3.6.14.0");
            var Q94;
            Q94=sQuery(id+"F0.wireOp",VERTEX,"E3.6.6.0");
            var Q95;
            Q95=makeQuery(id+"F1.opExtrude","SWEPT_BODY",BODY,{"disambiguationData":[OSD([sQuery(id+"F0.wireOp",EDGE,"E0.bottom"),sQuery(id+"F0.wireOp",EDGE,"E0.top"),sQuery(id+"F0.wireOp",EDGE,"E0.left"),sQuery(id+"F0.wireOp",EDGE,"E0.right")])]});
            hole(context, id + "F4", {"style" : HoleStyle.SIMPLE, "endStyle" : HoleEndStyle.THROUGH, "oppositeDirection" : true, "holeDiameter" : 6.35 * mm, "tappedDepth" : 12.7 * mm, "tapClearance" : 3, "startFromSketch" : true, "locations" : qUnion([Q0, Q1, Q2, Q3, Q4, Q5, Q6, Q7, Q8, Q9, Q10, Q11, Q12, Q13, Q14, Q15, Q16, Q17, Q18, Q19, Q20, Q21, Q22, Q23, Q24, Q25, Q26, Q27, Q28, Q29, Q30, Q31, Q32, Q33, Q34, Q35, Q36, Q37, Q38, Q39, Q40, Q41, Q42, Q43, Q44, Q45, Q46, Q47, Q48, Q49, Q50, Q51, Q52, Q53, Q54, Q55, Q56, Q57, Q58, Q59, Q60, Q61, Q62, Q63, Q64, Q65, Q66, Q67, Q68, Q69, Q70, Q71, Q72, Q73, Q74, Q75, Q76, Q77, Q78, Q79, Q80, Q81, Q82, Q83, Q84, Q85, Q86, Q87, Q88, Q89, Q90, Q91, Q92, Q93, Q94]), "scope" : qUnion([Q95])});
        }
        {
            var Q0;
            Q0=sQuery(id+"F0.wireOp",VERTEX,"E3.8.0.1");
            var Q1;
            Q1=sQuery(id+"F0.wireOp",VERTEX,"E3.7.3.1");
            var Q2;
            Q2=sQuery(id+"F0.wireOp",VERTEX,"E3.7.11.1");
            var Q3;
            Q3=sQuery(id+"F0.wireOp",VERTEX,"E3.9.13.1");
            var Q4;
            Q4=sQuery(id+"F0.wireOp",VERTEX,"E3.9.5.1");
            var Q5;
            Q5=sQuery(id+"F0.wireOp",VERTEX,"E3.8.16.1");
            var Q6;
            Q6=sQuery(id+"F0.wireOp",VERTEX,"E3.8.8.1");
            var Q7;
            Q7=sQuery(id+"F0.wireOp",VERTEX,"E3.8.1.0");
            var Q8;
            Q8=sQuery(id+"F0.wireOp",VERTEX,"E3.9.14.0");
            var Q9;
            Q9=sQuery(id+"F0.wireOp",VERTEX,"E3.9.6.0");
            var Q10;
            Q10=sQuery(id+"F0.wireOp",VERTEX,"E3.8.17.0");
            var Q11;
            Q11=sQuery(id+"F0.wireOp",VERTEX,"E3.8.9.0");
            var Q12;
            Q12=sQuery(id+"F0.wireOp",VERTEX,"E3.8.1.1");
            var Q13;
            Q13=sQuery(id+"F0.wireOp",VERTEX,"E3.7.12.1");
            var Q14;
            Q14=sQuery(id+"F0.wireOp",VERTEX,"E3.7.4.1");
            var Q15;
            Q15=sQuery(id+"F0.wireOp",VERTEX,"E3.9.14.1");
            var Q16;
            Q16=sQuery(id+"F0.wireOp",VERTEX,"E3.9.6.1");
            var Q17;
            Q17=sQuery(id+"F0.wireOp",VERTEX,"E3.8.17.1");
            var Q18;
            Q18=sQuery(id+"F0.wireOp",VERTEX,"E3.8.9.1");
            var Q19;
            Q19=sQuery(id+"F0.wireOp",VERTEX,"E3.8.2.0");
            var Q20;
            Q20=sQuery(id+"F0.wireOp",VERTEX,"E3.9.15.0");
            var Q21;
            Q21=sQuery(id+"F0.wireOp",VERTEX,"E3.9.7.0");
            var Q22;
            Q22=sQuery(id+"F0.wireOp",VERTEX,"E3.8.18.0");
            var Q23;
            Q23=sQuery(id+"F0.wireOp",VERTEX,"E3.8.10.0");
            var Q24;
            Q24=sQuery(id+"F0.wireOp",VERTEX,"E3.8.2.1");
            var Q25;
            Q25=sQuery(id+"F0.wireOp",VERTEX,"E3.7.13.1");
            var Q26;
            Q26=sQuery(id+"F0.wireOp",VERTEX,"E3.7.5.1");
            var Q27;
            Q27=sQuery(id+"F0.wireOp",VERTEX,"E3.9.15.1");
            var Q28;
            Q28=sQuery(id+"F0.wireOp",VERTEX,"E3.9.7.1");
            var Q29;
            Q29=sQuery(id+"F0.wireOp",VERTEX,"E3.8.18.1");
            var Q30;
            Q30=sQuery(id+"F0.wireOp",VERTEX,"E3.8.10.1");
            var Q31;
            Q31=sQuery(id+"F0.wireOp",VERTEX,"E3.8.3.0");
            var Q32;
            Q32=sQuery(id+"F0.wireOp",VERTEX,"E3.9.16.0");
            var Q33;
            Q33=sQuery(id+"F0.wireOp",VERTEX,"E3.9.8.0");
            var Q34;
            Q34=sQuery(id+"F0.wireOp",VERTEX,"E3.9.0.0");
            var Q35;
            Q35=sQuery(id+"F0.wireOp",VERTEX,"E3.8.11.0");
            var Q36;
            Q36=sQuery(id+"F0.wireOp",VERTEX,"E3.8.3.1");
            var Q37;
            Q37=sQuery(id+"F0.wireOp",VERTEX,"E3.7.14.1");
            var Q38;
            Q38=sQuery(id+"F0.wireOp",VERTEX,"E3.7.6.1");
            var Q39;
            Q39=sQuery(id+"F0.wireOp",VERTEX,"E3.9.16.1");
            var Q40;
            Q40=sQuery(id+"F0.wireOp",VERTEX,"E3.9.8.1");
            var Q41;
            Q41=sQuery(id+"F0.wireOp",VERTEX,"E3.9.0.1");
            var Q42;
            Q42=sQuery(id+"F0.wireOp",VERTEX,"E3.8.11.1");
            var Q43;
            Q43=sQuery(id+"F0.wireOp",VERTEX,"E3.8.4.0");
            var Q44;
            Q44=sQuery(id+"F0.wireOp",VERTEX,"E3.9.17.0");
            var Q45;
            Q45=sQuery(id+"F0.wireOp",VERTEX,"E3.9.9.0");
            var Q46;
            Q46=sQuery(id+"F0.wireOp",VERTEX,"E3.9.1.0");
            var Q47;
            Q47=sQuery(id+"F0.wireOp",VERTEX,"E3.8.12.0");
            var Q48;
            Q48=sQuery(id+"F0.wireOp",VERTEX,"E3.8.4.1");
            var Q49;
            Q49=sQuery(id+"F0.wireOp",VERTEX,"E3.7.15.1");
            var Q50;
            Q50=sQuery(id+"F0.wireOp",VERTEX,"E3.7.7.1");
            var Q51;
            Q51=sQuery(id+"F0.wireOp",VERTEX,"E3.9.17.1");
            var Q52;
            Q52=sQuery(id+"F0.wireOp",VERTEX,"E3.9.9.1");
            var Q53;
            Q53=sQuery(id+"F0.wireOp",VERTEX,"E3.9.1.1");
            var Q54;
            Q54=sQuery(id+"F0.wireOp",VERTEX,"E3.8.12.1");
            var Q55;
            Q55=sQuery(id+"F0.wireOp",VERTEX,"E3.8.5.0");
            var Q56;
            Q56=sQuery(id+"F0.wireOp",VERTEX,"E3.9.18.0");
            var Q57;
            Q57=sQuery(id+"F0.wireOp",VERTEX,"E3.9.10.0");
            var Q58;
            Q58=sQuery(id+"F0.wireOp",VERTEX,"E3.9.2.0");
            var Q59;
            Q59=sQuery(id+"F0.wireOp",VERTEX,"E3.8.13.0");
            var Q60;
            Q60=sQuery(id+"F0.wireOp",VERTEX,"E3.7.8.1");
            var Q61;
            Q61=sQuery(id+"F0.wireOp",VERTEX,"E3.7.0.1");
            var Q62;
            Q62=sQuery(id+"F0.wireOp",VERTEX,"E3.9.2.1");
            var Q63;
            Q63=sQuery(id+"F0.wireOp",VERTEX,"E3.8.13.1");
            var Q64;
            Q64=sQuery(id+"F0.wireOp",VERTEX,"E3.8.5.1");
            var Q65;
            Q65=sQuery(id+"F0.wireOp",VERTEX,"E3.7.16.1");
            var Q66;
            Q66=sQuery(id+"F0.wireOp",VERTEX,"E3.9.18.1");
            var Q67;
            Q67=sQuery(id+"F0.wireOp",VERTEX,"E3.9.10.1");
            var Q68;
            Q68=sQuery(id+"F0.wireOp",VERTEX,"E3.9.3.0");
            var Q69;
            Q69=sQuery(id+"F0.wireOp",VERTEX,"E3.8.14.0");
            var Q70;
            Q70=sQuery(id+"F0.wireOp",VERTEX,"E3.8.6.0");
            var Q71;
            Q71=sQuery(id+"F0.wireOp",VERTEX,"E3.9.11.0");
            var Q72;
            Q72=sQuery(id+"F0.wireOp",VERTEX,"E3.7.9.1");
            var Q73;
            Q73=sQuery(id+"F0.wireOp",VERTEX,"E3.7.1.1");
            var Q74;
            Q74=sQuery(id+"F0.wireOp",VERTEX,"E3.9.3.1");
            var Q75;
            Q75=sQuery(id+"F0.wireOp",VERTEX,"E3.8.14.1");
            var Q76;
            Q76=sQuery(id+"F0.wireOp",VERTEX,"E3.8.6.1");
            var Q77;
            Q77=sQuery(id+"F0.wireOp",VERTEX,"E3.7.17.1");
            var Q78;
            Q78=sQuery(id+"F0.wireOp",VERTEX,"E3.9.11.1");
            var Q79;
            Q79=sQuery(id+"F0.wireOp",VERTEX,"E3.9.4.0");
            var Q80;
            Q80=sQuery(id+"F0.wireOp",VERTEX,"E3.8.15.0");
            var Q81;
            Q81=sQuery(id+"F0.wireOp",VERTEX,"E3.8.7.0");
            var Q82;
            Q82=sQuery(id+"F0.wireOp",VERTEX,"E3.9.12.0");
            var Q83;
            Q83=sQuery(id+"F0.wireOp",VERTEX,"E3.9.12.1");
            var Q84;
            Q84=sQuery(id+"F0.wireOp",VERTEX,"E3.7.10.1");
            var Q85;
            Q85=sQuery(id+"F0.wireOp",VERTEX,"E3.7.2.1");
            var Q86;
            Q86=sQuery(id+"F0.wireOp",VERTEX,"E3.9.4.1");
            var Q87;
            Q87=sQuery(id+"F0.wireOp",VERTEX,"E3.8.15.1");
            var Q88;
            Q88=sQuery(id+"F0.wireOp",VERTEX,"E3.8.7.1");
            var Q89;
            Q89=sQuery(id+"F0.wireOp",VERTEX,"E3.7.18.1");
            var Q90;
            Q90=sQuery(id+"F0.wireOp",VERTEX,"E3.9.5.0");
            var Q91;
            Q91=sQuery(id+"F0.wireOp",VERTEX,"E3.8.16.0");
            var Q92;
            Q92=sQuery(id+"F0.wireOp",VERTEX,"E3.8.8.0");
            var Q93;
            Q93=sQuery(id+"F0.wireOp",VERTEX,"E3.8.0.0");
            var Q94;
            Q94=sQuery(id+"F0.wireOp",VERTEX,"E3.9.13.0");
            var Q95;
            Q95=makeQuery(id+"F1.opExtrude","SWEPT_BODY",BODY,{"disambiguationData":[OSD([sQuery(id+"F0.wireOp",EDGE,"E0.bottom"),sQuery(id+"F0.wireOp",EDGE,"E0.top"),sQuery(id+"F0.wireOp",EDGE,"E0.left"),sQuery(id+"F0.wireOp",EDGE,"E0.right")])]});
            hole(context, id + "F5", {"style" : HoleStyle.SIMPLE, "endStyle" : HoleEndStyle.THROUGH, "oppositeDirection" : true, "holeDiameter" : 6.35 * mm, "tappedDepth" : 12.7 * mm, "tapClearance" : 3, "startFromSketch" : true, "locations" : qUnion([Q0, Q1, Q2, Q3, Q4, Q5, Q6, Q7, Q8, Q9, Q10, Q11, Q12, Q13, Q14, Q15, Q16, Q17, Q18, Q19, Q20, Q21, Q22, Q23, Q24, Q25, Q26, Q27, Q28, Q29, Q30, Q31, Q32, Q33, Q34, Q35, Q36, Q37, Q38, Q39, Q40, Q41, Q42, Q43, Q44, Q45, Q46, Q47, Q48, Q49, Q50, Q51, Q52, Q53, Q54, Q55, Q56, Q57, Q58, Q59, Q60, Q61, Q62, Q63, Q64, Q65, Q66, Q67, Q68, Q69, Q70, Q71, Q72, Q73, Q74, Q75, Q76, Q77, Q78, Q79, Q80, Q81, Q82, Q83, Q84, Q85, Q86, Q87, Q88, Q89, Q90, Q91, Q92, Q93, Q94]), "scope" : qUnion([Q95])});
        }
        {
            var Q0;
            Q0=sQuery(id+"F0.wireOp",VERTEX,"E3.10.10.1");
            var Q1;
            Q1=sQuery(id+"F0.wireOp",VERTEX,"E3.10.2.1");
            var Q2;
            Q2=sQuery(id+"F0.wireOp",VERTEX,"E3.11.15.1");
            var Q3;
            Q3=sQuery(id+"F0.wireOp",VERTEX,"E3.11.7.1");
            var Q4;
            Q4=sQuery(id+"F0.wireOp",VERTEX,"E3.10.18.1");
            var Q5;
            Q5=sQuery(id+"F0.wireOp",VERTEX,"E3.10.11.0");
            var Q6;
            Q6=sQuery(id+"F0.wireOp",VERTEX,"E3.10.3.0");
            var Q7;
            Q7=sQuery(id+"F0.wireOp",VERTEX,"E3.12.5.0");
            var Q8;
            Q8=sQuery(id+"F0.wireOp",VERTEX,"E3.11.16.0");
            var Q9;
            Q9=sQuery(id+"F0.wireOp",VERTEX,"E3.11.8.0");
            var Q10;
            Q10=sQuery(id+"F0.wireOp",VERTEX,"E3.11.0.0");
            var Q11;
            Q11=sQuery(id+"F0.wireOp",VERTEX,"E3.12.13.0");
            var Q12;
            Q12=sQuery(id+"F0.wireOp",VERTEX,"E3.10.11.1");
            var Q13;
            Q13=sQuery(id+"F0.wireOp",VERTEX,"E3.10.3.1");
            var Q14;
            Q14=sQuery(id+"F0.wireOp",VERTEX,"E3.11.16.1");
            var Q15;
            Q15=sQuery(id+"F0.wireOp",VERTEX,"E3.11.8.1");
            var Q16;
            Q16=sQuery(id+"F0.wireOp",VERTEX,"E3.11.0.1");
            var Q17;
            Q17=sQuery(id+"F0.wireOp",VERTEX,"E3.12.14.0");
            var Q18;
            Q18=sQuery(id+"F0.wireOp",VERTEX,"E3.10.4.0");
            var Q19;
            Q19=sQuery(id+"F0.wireOp",VERTEX,"E3.10.12.0");
            var Q20;
            Q20=sQuery(id+"F0.wireOp",VERTEX,"E3.12.6.0");
            var Q21;
            Q21=sQuery(id+"F0.wireOp",VERTEX,"E3.11.17.0");
            var Q22;
            Q22=sQuery(id+"F0.wireOp",VERTEX,"E3.11.9.0");
            var Q23;
            Q23=sQuery(id+"F0.wireOp",VERTEX,"E3.11.1.0");
            var Q24;
            Q24=sQuery(id+"F0.wireOp",VERTEX,"E3.10.4.1");
            var Q25;
            Q25=sQuery(id+"F0.wireOp",VERTEX,"E3.10.12.1");
            var Q26;
            Q26=sQuery(id+"F0.wireOp",VERTEX,"E3.11.17.1");
            var Q27;
            Q27=sQuery(id+"F0.wireOp",VERTEX,"E3.11.9.1");
            var Q28;
            Q28=sQuery(id+"F0.wireOp",VERTEX,"E3.11.1.1");
            var Q29;
            Q29=sQuery(id+"F0.wireOp",VERTEX,"E3.10.5.0");
            var Q30;
            Q30=sQuery(id+"F0.wireOp",VERTEX,"E3.10.13.0");
            var Q31;
            Q31=sQuery(id+"F0.wireOp",VERTEX,"E3.12.7.0");
            var Q32;
            Q32=sQuery(id+"F0.wireOp",VERTEX,"E3.11.18.0");
            var Q33;
            Q33=sQuery(id+"F0.wireOp",VERTEX,"E3.11.10.0");
            var Q34;
            Q34=sQuery(id+"F0.wireOp",VERTEX,"E3.11.2.0");
            var Q35;
            Q35=sQuery(id+"F0.wireOp",VERTEX,"E3.12.15.0");
            var Q36;
            Q36=sQuery(id+"F0.wireOp",VERTEX,"E3.10.5.1");
            var Q37;
            Q37=sQuery(id+"F0.wireOp",VERTEX,"E3.10.13.1");
            var Q38;
            Q38=sQuery(id+"F0.wireOp",VERTEX,"E3.11.18.1");
            var Q39;
            Q39=sQuery(id+"F0.wireOp",VERTEX,"E3.11.10.1");
            var Q40;
            Q40=sQuery(id+"F0.wireOp",VERTEX,"E3.11.2.1");
            var Q41;
            Q41=sQuery(id+"F0.wireOp",VERTEX,"E3.10.6.0");
            var Q42;
            Q42=sQuery(id+"F0.wireOp",VERTEX,"E3.10.14.0");
            var Q43;
            Q43=sQuery(id+"F0.wireOp",VERTEX,"E3.12.8.0");
            var Q44;
            Q44=sQuery(id+"F0.wireOp",VERTEX,"E3.12.0.0");
            var Q45;
            Q45=sQuery(id+"F0.wireOp",VERTEX,"E3.11.11.0");
            var Q46;
            Q46=sQuery(id+"F0.wireOp",VERTEX,"E3.11.3.0");
            var Q47;
            Q47=sQuery(id+"F0.wireOp",VERTEX,"E3.12.16.0");
            var Q48;
            Q48=sQuery(id+"F0.wireOp",VERTEX,"E3.10.6.1");
            var Q49;
            Q49=sQuery(id+"F0.wireOp",VERTEX,"E3.10.14.1");
            var Q50;
            Q50=sQuery(id+"F0.wireOp",VERTEX,"E3.11.11.1");
            var Q51;
            Q51=sQuery(id+"F0.wireOp",VERTEX,"E3.11.3.1");
            var Q52;
            Q52=sQuery(id+"F0.wireOp",VERTEX,"E3.10.7.0");
            var Q53;
            Q53=sQuery(id+"F0.wireOp",VERTEX,"E3.10.15.0");
            var Q54;
            Q54=sQuery(id+"F0.wireOp",VERTEX,"E3.12.9.0");
            var Q55;
            Q55=sQuery(id+"F0.wireOp",VERTEX,"E3.12.1.0");
            var Q56;
            Q56=sQuery(id+"F0.wireOp",VERTEX,"E3.11.12.0");
            var Q57;
            Q57=sQuery(id+"F0.wireOp",VERTEX,"E3.11.4.0");
            var Q58;
            Q58=sQuery(id+"F0.wireOp",VERTEX,"E3.12.17.0");
            var Q59;
            Q59=sQuery(id+"F0.wireOp",VERTEX,"E3.10.7.1");
            var Q60;
            Q60=sQuery(id+"F0.wireOp",VERTEX,"E3.11.12.1");
            var Q61;
            Q61=sQuery(id+"F0.wireOp",VERTEX,"E3.11.4.1");
            var Q62;
            Q62=sQuery(id+"F0.wireOp",VERTEX,"E3.10.15.1");
            var Q63;
            Q63=sQuery(id+"F0.wireOp",VERTEX,"E3.10.8.0");
            var Q64;
            Q64=sQuery(id+"F0.wireOp",VERTEX,"E3.10.0.0");
            var Q65;
            Q65=sQuery(id+"F0.wireOp",VERTEX,"E3.11.13.0");
            var Q66;
            Q66=sQuery(id+"F0.wireOp",VERTEX,"E3.11.5.0");
            var Q67;
            Q67=sQuery(id+"F0.wireOp",VERTEX,"E3.10.16.0");
            var Q68;
            Q68=sQuery(id+"F0.wireOp",VERTEX,"E3.12.18.0");
            var Q69;
            Q69=sQuery(id+"F0.wireOp",VERTEX,"E3.12.10.0");
            var Q70;
            Q70=sQuery(id+"F0.wireOp",VERTEX,"E3.12.2.0");
            var Q71;
            Q71=sQuery(id+"F0.wireOp",VERTEX,"E3.10.8.1");
            var Q72;
            Q72=sQuery(id+"F0.wireOp",VERTEX,"E3.10.0.1");
            var Q73;
            Q73=sQuery(id+"F0.wireOp",VERTEX,"E3.11.13.1");
            var Q74;
            Q74=sQuery(id+"F0.wireOp",VERTEX,"E3.11.5.1");
            var Q75;
            Q75=sQuery(id+"F0.wireOp",VERTEX,"E3.10.16.1");
            var Q76;
            Q76=sQuery(id+"F0.wireOp",VERTEX,"E3.10.9.0");
            var Q77;
            Q77=sQuery(id+"F0.wireOp",VERTEX,"E3.10.1.0");
            var Q78;
            Q78=sQuery(id+"F0.wireOp",VERTEX,"E3.11.14.0");
            var Q79;
            Q79=sQuery(id+"F0.wireOp",VERTEX,"E3.11.6.0");
            var Q80;
            Q80=sQuery(id+"F0.wireOp",VERTEX,"E3.10.17.0");
            var Q81;
            Q81=sQuery(id+"F0.wireOp",VERTEX,"E3.12.11.0");
            var Q82;
            Q82=sQuery(id+"F0.wireOp",VERTEX,"E3.12.3.0");
            var Q83;
            Q83=sQuery(id+"F0.wireOp",VERTEX,"E3.10.9.1");
            var Q84;
            Q84=sQuery(id+"F0.wireOp",VERTEX,"E3.10.1.1");
            var Q85;
            Q85=sQuery(id+"F0.wireOp",VERTEX,"E3.11.14.1");
            var Q86;
            Q86=sQuery(id+"F0.wireOp",VERTEX,"E3.11.6.1");
            var Q87;
            Q87=sQuery(id+"F0.wireOp",VERTEX,"E3.10.17.1");
            var Q88;
            Q88=sQuery(id+"F0.wireOp",VERTEX,"E3.11.15.0");
            var Q89;
            Q89=sQuery(id+"F0.wireOp",VERTEX,"E3.11.7.0");
            var Q90;
            Q90=sQuery(id+"F0.wireOp",VERTEX,"E3.10.18.0");
            var Q91;
            Q91=sQuery(id+"F0.wireOp",VERTEX,"E3.12.12.0");
            var Q92;
            Q92=sQuery(id+"F0.wireOp",VERTEX,"E3.12.4.0");
            var Q93;
            Q93=sQuery(id+"F0.wireOp",VERTEX,"E3.10.10.0");
            var Q94;
            Q94=sQuery(id+"F0.wireOp",VERTEX,"E3.10.2.0");
            var Q95;
            Q95=makeQuery(id+"F1.opExtrude","SWEPT_BODY",BODY,{"disambiguationData":[OSD([sQuery(id+"F0.wireOp",EDGE,"E0.bottom"),sQuery(id+"F0.wireOp",EDGE,"E0.top"),sQuery(id+"F0.wireOp",EDGE,"E0.left"),sQuery(id+"F0.wireOp",EDGE,"E0.right")])]});
            hole(context, id + "F6", {"style" : HoleStyle.SIMPLE, "endStyle" : HoleEndStyle.THROUGH, "oppositeDirection" : true, "holeDiameter" : 6.35 * mm, "tappedDepth" : 12.7 * mm, "tapClearance" : 3, "startFromSketch" : true, "locations" : qUnion([Q0, Q1, Q2, Q3, Q4, Q5, Q6, Q7, Q8, Q9, Q10, Q11, Q12, Q13, Q14, Q15, Q16, Q17, Q18, Q19, Q20, Q21, Q22, Q23, Q24, Q25, Q26, Q27, Q28, Q29, Q30, Q31, Q32, Q33, Q34, Q35, Q36, Q37, Q38, Q39, Q40, Q41, Q42, Q43, Q44, Q45, Q46, Q47, Q48, Q49, Q50, Q51, Q52, Q53, Q54, Q55, Q56, Q57, Q58, Q59, Q60, Q61, Q62, Q63, Q64, Q65, Q66, Q67, Q68, Q69, Q70, Q71, Q72, Q73, Q74, Q75, Q76, Q77, Q78, Q79, Q80, Q81, Q82, Q83, Q84, Q85, Q86, Q87, Q88, Q89, Q90, Q91, Q92, Q93, Q94]), "scope" : qUnion([Q95])});
        }
        {
            var Q0;
            Q0=sQuery(id+"F0.wireOp",VERTEX,"E3.12.4.1");
            var Q1;
            Q1=sQuery(id+"F0.wireOp",VERTEX,"E3.13.17.1");
            var Q2;
            Q2=sQuery(id+"F0.wireOp",VERTEX,"E3.13.9.1");
            var Q3;
            Q3=sQuery(id+"F0.wireOp",VERTEX,"E3.13.1.1");
            var Q4;
            Q4=sQuery(id+"F0.wireOp",VERTEX,"E3.12.12.1");
            var Q5;
            Q5=sQuery(id+"F0.wireOp",VERTEX,"E3.14.14.1");
            var Q6;
            Q6=sQuery(id+"F0.wireOp",VERTEX,"E3.14.6.1");
            var Q7;
            Q7=sQuery(id+"F0.wireOp",VERTEX,"E3.13.18.0");
            var Q8;
            Q8=sQuery(id+"F0.wireOp",VERTEX,"E3.13.10.0");
            var Q9;
            Q9=sQuery(id+"F0.wireOp",VERTEX,"E3.13.2.0");
            var Q10;
            Q10=sQuery(id+"F0.wireOp",VERTEX,"E3.14.15.0");
            var Q11;
            Q11=sQuery(id+"F0.wireOp",VERTEX,"E3.14.7.0");
            var Q12;
            Q12=sQuery(id+"F0.wireOp",VERTEX,"E3.12.5.1");
            var Q13;
            Q13=sQuery(id+"F0.wireOp",VERTEX,"E3.13.18.1");
            var Q14;
            Q14=sQuery(id+"F0.wireOp",VERTEX,"E3.13.10.1");
            var Q15;
            Q15=sQuery(id+"F0.wireOp",VERTEX,"E3.13.2.1");
            var Q16;
            Q16=sQuery(id+"F0.wireOp",VERTEX,"E3.12.13.1");
            var Q17;
            Q17=sQuery(id+"F0.wireOp",VERTEX,"E3.14.15.1");
            var Q18;
            Q18=sQuery(id+"F0.wireOp",VERTEX,"E3.14.7.1");
            var Q19;
            Q19=sQuery(id+"F0.wireOp",VERTEX,"E3.14.0.0");
            var Q20;
            Q20=sQuery(id+"F0.wireOp",VERTEX,"E3.13.11.0");
            var Q21;
            Q21=sQuery(id+"F0.wireOp",VERTEX,"E3.13.3.0");
            var Q22;
            Q22=sQuery(id+"F0.wireOp",VERTEX,"E3.14.16.0");
            var Q23;
            Q23=sQuery(id+"F0.wireOp",VERTEX,"E3.14.8.0");
            var Q24;
            Q24=sQuery(id+"F0.wireOp",VERTEX,"E3.14.16.1");
            var Q25;
            Q25=sQuery(id+"F0.wireOp",VERTEX,"E3.14.8.1");
            var Q26;
            Q26=sQuery(id+"F0.wireOp",VERTEX,"E3.12.6.1");
            var Q27;
            Q27=sQuery(id+"F0.wireOp",VERTEX,"E3.14.0.1");
            var Q28;
            Q28=sQuery(id+"F0.wireOp",VERTEX,"E3.13.11.1");
            var Q29;
            Q29=sQuery(id+"F0.wireOp",VERTEX,"E3.13.3.1");
            var Q30;
            Q30=sQuery(id+"F0.wireOp",VERTEX,"E3.12.14.1");
            var Q31;
            Q31=sQuery(id+"F0.wireOp",VERTEX,"E3.14.1.0");
            var Q32;
            Q32=sQuery(id+"F0.wireOp",VERTEX,"E3.13.12.0");
            var Q33;
            Q33=sQuery(id+"F0.wireOp",VERTEX,"E3.13.4.0");
            var Q34;
            Q34=sQuery(id+"F0.wireOp",VERTEX,"E3.14.17.0");
            var Q35;
            Q35=sQuery(id+"F0.wireOp",VERTEX,"E3.14.9.0");
            var Q36;
            Q36=sQuery(id+"F0.wireOp",VERTEX,"E3.12.7.1");
            var Q37;
            Q37=sQuery(id+"F0.wireOp",VERTEX,"E3.14.1.1");
            var Q38;
            Q38=sQuery(id+"F0.wireOp",VERTEX,"E3.13.12.1");
            var Q39;
            Q39=sQuery(id+"F0.wireOp",VERTEX,"E3.13.4.1");
            var Q40;
            Q40=sQuery(id+"F0.wireOp",VERTEX,"E3.12.15.1");
            var Q41;
            Q41=sQuery(id+"F0.wireOp",VERTEX,"E3.14.17.1");
            var Q42;
            Q42=sQuery(id+"F0.wireOp",VERTEX,"E3.14.9.1");
            var Q43;
            Q43=sQuery(id+"F0.wireOp",VERTEX,"E3.14.2.0");
            var Q44;
            Q44=sQuery(id+"F0.wireOp",VERTEX,"E3.13.13.0");
            var Q45;
            Q45=sQuery(id+"F0.wireOp",VERTEX,"E3.13.5.0");
            var Q46;
            Q46=sQuery(id+"F0.wireOp",VERTEX,"E3.14.18.0");
            var Q47;
            Q47=sQuery(id+"F0.wireOp",VERTEX,"E3.14.10.0");
            var Q48;
            Q48=sQuery(id+"F0.wireOp",VERTEX,"E3.12.8.1");
            var Q49;
            Q49=sQuery(id+"F0.wireOp",VERTEX,"E3.12.0.1");
            var Q50;
            Q50=sQuery(id+"F0.wireOp",VERTEX,"E3.14.2.1");
            var Q51;
            Q51=sQuery(id+"F0.wireOp",VERTEX,"E3.13.13.1");
            var Q52;
            Q52=sQuery(id+"F0.wireOp",VERTEX,"E3.13.5.1");
            var Q53;
            Q53=sQuery(id+"F0.wireOp",VERTEX,"E3.12.16.1");
            var Q54;
            Q54=sQuery(id+"F0.wireOp",VERTEX,"E3.14.18.1");
            var Q55;
            Q55=sQuery(id+"F0.wireOp",VERTEX,"E3.14.10.1");
            var Q56;
            Q56=sQuery(id+"F0.wireOp",VERTEX,"E3.14.3.0");
            var Q57;
            Q57=sQuery(id+"F0.wireOp",VERTEX,"E3.13.14.0");
            var Q58;
            Q58=sQuery(id+"F0.wireOp",VERTEX,"E3.13.6.0");
            var Q59;
            Q59=sQuery(id+"F0.wireOp",VERTEX,"E3.14.11.0");
            var Q60;
            Q60=sQuery(id+"F0.wireOp",VERTEX,"E3.13.6.1");
            var Q61;
            Q61=sQuery(id+"F0.wireOp",VERTEX,"E3.12.17.1");
            var Q62;
            Q62=sQuery(id+"F0.wireOp",VERTEX,"E3.12.9.1");
            var Q63;
            Q63=sQuery(id+"F0.wireOp",VERTEX,"E3.12.1.1");
            var Q64;
            Q64=sQuery(id+"F0.wireOp",VERTEX,"E3.14.11.1");
            var Q65;
            Q65=sQuery(id+"F0.wireOp",VERTEX,"E3.14.3.1");
            var Q66;
            Q66=sQuery(id+"F0.wireOp",VERTEX,"E3.13.14.1");
            var Q67;
            Q67=sQuery(id+"F0.wireOp",VERTEX,"E3.13.7.0");
            var Q68;
            Q68=sQuery(id+"F0.wireOp",VERTEX,"E3.14.12.0");
            var Q69;
            Q69=sQuery(id+"F0.wireOp",VERTEX,"E3.14.4.0");
            var Q70;
            Q70=sQuery(id+"F0.wireOp",VERTEX,"E3.13.15.0");
            var Q71;
            Q71=sQuery(id+"F0.wireOp",VERTEX,"E3.13.7.1");
            var Q72;
            Q72=sQuery(id+"F0.wireOp",VERTEX,"E3.12.18.1");
            var Q73;
            Q73=sQuery(id+"F0.wireOp",VERTEX,"E3.12.10.1");
            var Q74;
            Q74=sQuery(id+"F0.wireOp",VERTEX,"E3.12.2.1");
            var Q75;
            Q75=sQuery(id+"F0.wireOp",VERTEX,"E3.14.12.1");
            var Q76;
            Q76=sQuery(id+"F0.wireOp",VERTEX,"E3.14.4.1");
            var Q77;
            Q77=sQuery(id+"F0.wireOp",VERTEX,"E3.13.15.1");
            var Q78;
            Q78=sQuery(id+"F0.wireOp",VERTEX,"E3.13.8.0");
            var Q79;
            Q79=sQuery(id+"F0.wireOp",VERTEX,"E3.13.0.0");
            var Q80;
            Q80=sQuery(id+"F0.wireOp",VERTEX,"E3.14.13.0");
            var Q81;
            Q81=sQuery(id+"F0.wireOp",VERTEX,"E3.14.5.0");
            var Q82;
            Q82=sQuery(id+"F0.wireOp",VERTEX,"E3.13.16.0");
            var Q83;
            Q83=sQuery(id+"F0.wireOp",VERTEX,"E3.13.8.1");
            var Q84;
            Q84=sQuery(id+"F0.wireOp",VERTEX,"E3.13.0.1");
            var Q85;
            Q85=sQuery(id+"F0.wireOp",VERTEX,"E3.12.11.1");
            var Q86;
            Q86=sQuery(id+"F0.wireOp",VERTEX,"E3.12.3.1");
            var Q87;
            Q87=sQuery(id+"F0.wireOp",VERTEX,"E3.14.13.1");
            var Q88;
            Q88=sQuery(id+"F0.wireOp",VERTEX,"E3.14.5.1");
            var Q89;
            Q89=sQuery(id+"F0.wireOp",VERTEX,"E3.13.16.1");
            var Q90;
            Q90=sQuery(id+"F0.wireOp",VERTEX,"E3.13.9.0");
            var Q91;
            Q91=sQuery(id+"F0.wireOp",VERTEX,"E3.13.1.0");
            var Q92;
            Q92=sQuery(id+"F0.wireOp",VERTEX,"E3.14.14.0");
            var Q93;
            Q93=sQuery(id+"F0.wireOp",VERTEX,"E3.14.6.0");
            var Q94;
            Q94=sQuery(id+"F0.wireOp",VERTEX,"E3.13.17.0");
            var Q95;
            Q95=makeQuery(id+"F1.opExtrude","SWEPT_BODY",BODY,{"disambiguationData":[OSD([sQuery(id+"F0.wireOp",EDGE,"E0.bottom"),sQuery(id+"F0.wireOp",EDGE,"E0.top"),sQuery(id+"F0.wireOp",EDGE,"E0.left"),sQuery(id+"F0.wireOp",EDGE,"E0.right")])]});
            hole(context, id + "F7", {"style" : HoleStyle.SIMPLE, "endStyle" : HoleEndStyle.THROUGH, "oppositeDirection" : true, "holeDiameter" : 6.35 * mm, "tappedDepth" : 12.7 * mm, "tapClearance" : 3, "startFromSketch" : true, "locations" : qUnion([Q0, Q1, Q2, Q3, Q4, Q5, Q6, Q7, Q8, Q9, Q10, Q11, Q12, Q13, Q14, Q15, Q16, Q17, Q18, Q19, Q20, Q21, Q22, Q23, Q24, Q25, Q26, Q27, Q28, Q29, Q30, Q31, Q32, Q33, Q34, Q35, Q36, Q37, Q38, Q39, Q40, Q41, Q42, Q43, Q44, Q45, Q46, Q47, Q48, Q49, Q50, Q51, Q52, Q53, Q54, Q55, Q56, Q57, Q58, Q59, Q60, Q61, Q62, Q63, Q64, Q65, Q66, Q67, Q68, Q69, Q70, Q71, Q72, Q73, Q74, Q75, Q76, Q77, Q78, Q79, Q80, Q81, Q82, Q83, Q84, Q85, Q86, Q87, Q88, Q89, Q90, Q91, Q92, Q93, Q94]), "scope" : qUnion([Q95])});
        }
        {
            var Q0;
            Q0=sQuery(id+"F0.wireOp",VERTEX,"E3.15.11.1");
            var Q1;
            Q1=sQuery(id+"F0.wireOp",VERTEX,"E3.15.3.1");
            var Q2;
            Q2=sQuery(id+"F0.wireOp",VERTEX,"E3.16.16.1");
            var Q3;
            Q3=sQuery(id+"F0.wireOp",VERTEX,"E3.16.8.1");
            var Q4;
            Q4=sQuery(id+"F0.wireOp",VERTEX,"E3.16.0.1");
            var Q5;
            Q5=sQuery(id+"F0.wireOp",VERTEX,"E3.15.12.0");
            var Q6;
            Q6=sQuery(id+"F0.wireOp",VERTEX,"E3.15.4.0");
            var Q7;
            Q7=sQuery(id+"F0.wireOp",VERTEX,"E3.17.6.0");
            var Q8;
            Q8=sQuery(id+"F0.wireOp",VERTEX,"E3.16.17.0");
            var Q9;
            Q9=sQuery(id+"F0.wireOp",VERTEX,"E3.16.9.0");
            var Q10;
            Q10=sQuery(id+"F0.wireOp",VERTEX,"E3.16.1.0");
            var Q11;
            Q11=sQuery(id+"F0.wireOp",VERTEX,"E3.17.14.0");
            var Q12;
            Q12=sQuery(id+"F0.wireOp",VERTEX,"E3.15.12.1");
            var Q13;
            Q13=sQuery(id+"F0.wireOp",VERTEX,"E3.15.4.1");
            var Q14;
            Q14=sQuery(id+"F0.wireOp",VERTEX,"E3.16.17.1");
            var Q15;
            Q15=sQuery(id+"F0.wireOp",VERTEX,"E3.16.9.1");
            var Q16;
            Q16=sQuery(id+"F0.wireOp",VERTEX,"E3.16.1.1");
            var Q17;
            Q17=sQuery(id+"F0.wireOp",VERTEX,"E3.15.13.0");
            var Q18;
            Q18=sQuery(id+"F0.wireOp",VERTEX,"E3.15.5.0");
            var Q19;
            Q19=sQuery(id+"F0.wireOp",VERTEX,"E3.17.7.0");
            var Q20;
            Q20=sQuery(id+"F0.wireOp",VERTEX,"E3.16.18.0");
            var Q21;
            Q21=sQuery(id+"F0.wireOp",VERTEX,"E3.16.10.0");
            var Q22;
            Q22=sQuery(id+"F0.wireOp",VERTEX,"E3.16.2.0");
            var Q23;
            Q23=sQuery(id+"F0.wireOp",VERTEX,"E3.17.15.0");
            var Q24;
            Q24=sQuery(id+"F0.wireOp",VERTEX,"E3.15.13.1");
            var Q25;
            Q25=sQuery(id+"F0.wireOp",VERTEX,"E3.15.5.1");
            var Q26;
            Q26=sQuery(id+"F0.wireOp",VERTEX,"E3.16.18.1");
            var Q27;
            Q27=sQuery(id+"F0.wireOp",VERTEX,"E3.16.10.1");
            var Q28;
            Q28=sQuery(id+"F0.wireOp",VERTEX,"E3.16.2.1");
            var Q29;
            Q29=sQuery(id+"F0.wireOp",VERTEX,"E3.17.8.0");
            var Q30;
            Q30=sQuery(id+"F0.wireOp",VERTEX,"E3.17.0.0");
            var Q31;
            Q31=sQuery(id+"F0.wireOp",VERTEX,"E3.16.11.0");
            var Q32;
            Q32=sQuery(id+"F0.wireOp",VERTEX,"E3.16.3.0");
            var Q33;
            Q33=sQuery(id+"F0.wireOp",VERTEX,"E3.17.16.0");
            var Q34;
            Q34=sQuery(id+"F0.wireOp",VERTEX,"E3.15.14.0");
            var Q35;
            Q35=sQuery(id+"F0.wireOp",VERTEX,"E3.15.6.0");
            var Q36;
            Q36=sQuery(id+"F0.wireOp",VERTEX,"E3.15.14.1");
            var Q37;
            Q37=sQuery(id+"F0.wireOp",VERTEX,"E3.15.6.1");
            var Q38;
            Q38=sQuery(id+"F0.wireOp",VERTEX,"E3.16.11.1");
            var Q39;
            Q39=sQuery(id+"F0.wireOp",VERTEX,"E3.16.3.1");
            var Q40;
            Q40=sQuery(id+"F0.wireOp",VERTEX,"E3.15.15.0");
            var Q41;
            Q41=sQuery(id+"F0.wireOp",VERTEX,"E3.15.7.0");
            var Q42;
            Q42=sQuery(id+"F0.wireOp",VERTEX,"E3.17.9.0");
            var Q43;
            Q43=sQuery(id+"F0.wireOp",VERTEX,"E3.17.1.0");
            var Q44;
            Q44=sQuery(id+"F0.wireOp",VERTEX,"E3.16.12.0");
            var Q45;
            Q45=sQuery(id+"F0.wireOp",VERTEX,"E3.16.4.0");
            var Q46;
            Q46=sQuery(id+"F0.wireOp",VERTEX,"E3.17.17.0");
            var Q47;
            Q47=sQuery(id+"F0.wireOp",VERTEX,"E3.15.15.1");
            var Q48;
            Q48=sQuery(id+"F0.wireOp",VERTEX,"E3.15.7.1");
            var Q49;
            Q49=sQuery(id+"F0.wireOp",VERTEX,"E3.16.12.1");
            var Q50;
            Q50=sQuery(id+"F0.wireOp",VERTEX,"E3.16.4.1");
            var Q51;
            Q51=sQuery(id+"F0.wireOp",VERTEX,"E3.15.16.0");
            var Q52;
            Q52=sQuery(id+"F0.wireOp",VERTEX,"E3.15.8.0");
            var Q53;
            Q53=sQuery(id+"F0.wireOp",VERTEX,"E3.15.0.0");
            var Q54;
            Q54=sQuery(id+"F0.wireOp",VERTEX,"E3.17.10.0");
            var Q55;
            Q55=sQuery(id+"F0.wireOp",VERTEX,"E3.17.2.0");
            var Q56;
            Q56=sQuery(id+"F0.wireOp",VERTEX,"E3.16.13.0");
            var Q57;
            Q57=sQuery(id+"F0.wireOp",VERTEX,"E3.16.5.0");
            var Q58;
            Q58=sQuery(id+"F0.wireOp",VERTEX,"E3.17.18.0");
            var Q59;
            Q59=sQuery(id+"F0.wireOp",VERTEX,"E3.15.0.1");
            var Q60;
            Q60=sQuery(id+"F0.wireOp",VERTEX,"E3.16.13.1");
            var Q61;
            Q61=sQuery(id+"F0.wireOp",VERTEX,"E3.16.5.1");
            var Q62;
            Q62=sQuery(id+"F0.wireOp",VERTEX,"E3.15.16.1");
            var Q63;
            Q63=sQuery(id+"F0.wireOp",VERTEX,"E3.15.8.1");
            var Q64;
            Q64=sQuery(id+"F0.wireOp",VERTEX,"E3.15.1.0");
            var Q65;
            Q65=sQuery(id+"F0.wireOp",VERTEX,"E3.16.14.0");
            var Q66;
            Q66=sQuery(id+"F0.wireOp",VERTEX,"E3.16.6.0");
            var Q67;
            Q67=sQuery(id+"F0.wireOp",VERTEX,"E3.15.17.0");
            var Q68;
            Q68=sQuery(id+"F0.wireOp",VERTEX,"E3.15.9.0");
            var Q69;
            Q69=sQuery(id+"F0.wireOp",VERTEX,"E3.17.11.0");
            var Q70;
            Q70=sQuery(id+"F0.wireOp",VERTEX,"E3.17.3.0");
            var Q71;
            Q71=sQuery(id+"F0.wireOp",VERTEX,"E3.15.1.1");
            var Q72;
            Q72=sQuery(id+"F0.wireOp",VERTEX,"E3.16.14.1");
            var Q73;
            Q73=sQuery(id+"F0.wireOp",VERTEX,"E3.16.6.1");
            var Q74;
            Q74=sQuery(id+"F0.wireOp",VERTEX,"E3.15.17.1");
            var Q75;
            Q75=sQuery(id+"F0.wireOp",VERTEX,"E3.15.9.1");
            var Q76;
            Q76=sQuery(id+"F0.wireOp",VERTEX,"E3.15.2.0");
            var Q77;
            Q77=sQuery(id+"F0.wireOp",VERTEX,"E3.16.15.0");
            var Q78;
            Q78=sQuery(id+"F0.wireOp",VERTEX,"E3.16.7.0");
            var Q79;
            Q79=sQuery(id+"F0.wireOp",VERTEX,"E3.15.18.0");
            var Q80;
            Q80=sQuery(id+"F0.wireOp",VERTEX,"E3.15.10.0");
            var Q81;
            Q81=sQuery(id+"F0.wireOp",VERTEX,"E3.17.12.0");
            var Q82;
            Q82=sQuery(id+"F0.wireOp",VERTEX,"E3.17.4.0");
            var Q83;
            Q83=sQuery(id+"F0.wireOp",VERTEX,"E3.15.2.1");
            var Q84;
            Q84=sQuery(id+"F0.wireOp",VERTEX,"E3.16.15.1");
            var Q85;
            Q85=sQuery(id+"F0.wireOp",VERTEX,"E3.16.7.1");
            var Q86;
            Q86=sQuery(id+"F0.wireOp",VERTEX,"E3.15.18.1");
            var Q87;
            Q87=sQuery(id+"F0.wireOp",VERTEX,"E3.15.10.1");
            var Q88;
            Q88=sQuery(id+"F0.wireOp",VERTEX,"E3.15.3.0");
            var Q89;
            Q89=sQuery(id+"F0.wireOp",VERTEX,"E3.16.16.0");
            var Q90;
            Q90=sQuery(id+"F0.wireOp",VERTEX,"E3.16.8.0");
            var Q91;
            Q91=sQuery(id+"F0.wireOp",VERTEX,"E3.16.0.0");
            var Q92;
            Q92=sQuery(id+"F0.wireOp",VERTEX,"E3.15.11.0");
            var Q93;
            Q93=sQuery(id+"F0.wireOp",VERTEX,"E3.17.13.0");
            var Q94;
            Q94=sQuery(id+"F0.wireOp",VERTEX,"E3.17.5.0");
            var Q95;
            Q95=makeQuery(id+"F1.opExtrude","SWEPT_BODY",BODY,{"disambiguationData":[OSD([sQuery(id+"F0.wireOp",EDGE,"E0.bottom"),sQuery(id+"F0.wireOp",EDGE,"E0.top"),sQuery(id+"F0.wireOp",EDGE,"E0.left"),sQuery(id+"F0.wireOp",EDGE,"E0.right")])]});
            hole(context, id + "F8", {"style" : HoleStyle.SIMPLE, "endStyle" : HoleEndStyle.THROUGH, "oppositeDirection" : true, "holeDiameter" : 6.35 * mm, "tappedDepth" : 12.7 * mm, "tapClearance" : 3, "startFromSketch" : true, "locations" : qUnion([Q0, Q1, Q2, Q3, Q4, Q5, Q6, Q7, Q8, Q9, Q10, Q11, Q12, Q13, Q14, Q15, Q16, Q17, Q18, Q19, Q20, Q21, Q22, Q23, Q24, Q25, Q26, Q27, Q28, Q29, Q30, Q31, Q32, Q33, Q34, Q35, Q36, Q37, Q38, Q39, Q40, Q41, Q42, Q43, Q44, Q45, Q46, Q47, Q48, Q49, Q50, Q51, Q52, Q53, Q54, Q55, Q56, Q57, Q58, Q59, Q60, Q61, Q62, Q63, Q64, Q65, Q66, Q67, Q68, Q69, Q70, Q71, Q72, Q73, Q74, Q75, Q76, Q77, Q78, Q79, Q80, Q81, Q82, Q83, Q84, Q85, Q86, Q87, Q88, Q89, Q90, Q91, Q92, Q93, Q94]), "scope" : qUnion([Q95])});
        }
        {
            var Q0;
            Q0=sQuery(id+"F0.wireOp",VERTEX,"E3.19.15.1");
            var Q1;
            Q1=sQuery(id+"F0.wireOp",VERTEX,"E3.19.7.1");
            var Q2;
            Q2=sQuery(id+"F0.wireOp",VERTEX,"E3.17.5.1");
            var Q3;
            Q3=sQuery(id+"F0.wireOp",VERTEX,"E3.18.18.1");
            var Q4;
            Q4=sQuery(id+"F0.wireOp",VERTEX,"E3.18.10.1");
            var Q5;
            Q5=sQuery(id+"F0.wireOp",VERTEX,"E3.18.2.1");
            var Q6;
            Q6=sQuery(id+"F0.wireOp",VERTEX,"E3.17.13.1");
            var Q7;
            Q7=sQuery(id+"F0.wireOp",VERTEX,"E3.19.0.0");
            var Q8;
            Q8=sQuery(id+"F0.wireOp",VERTEX,"E3.18.11.0");
            var Q9;
            Q9=sQuery(id+"F0.wireOp",VERTEX,"E3.18.3.0");
            var Q10;
            Q10=sQuery(id+"F0.wireOp",VERTEX,"E3.19.16.0");
            var Q11;
            Q11=sQuery(id+"F0.wireOp",VERTEX,"E3.19.8.0");
            var Q12;
            Q12=sQuery(id+"F0.wireOp",VERTEX,"E3.17.6.1");
            var Q13;
            Q13=sQuery(id+"F0.wireOp",VERTEX,"E3.19.0.1");
            var Q14;
            Q14=sQuery(id+"F0.wireOp",VERTEX,"E3.18.11.1");
            var Q15;
            Q15=sQuery(id+"F0.wireOp",VERTEX,"E3.18.3.1");
            var Q16;
            Q16=sQuery(id+"F0.wireOp",VERTEX,"E3.17.14.1");
            var Q17;
            Q17=sQuery(id+"F0.wireOp",VERTEX,"E3.19.16.1");
            var Q18;
            Q18=sQuery(id+"F0.wireOp",VERTEX,"E3.19.8.1");
            var Q19;
            Q19=sQuery(id+"F0.wireOp",VERTEX,"E3.19.1.0");
            var Q20;
            Q20=sQuery(id+"F0.wireOp",VERTEX,"E3.18.12.0");
            var Q21;
            Q21=sQuery(id+"F0.wireOp",VERTEX,"E3.18.4.0");
            var Q22;
            Q22=sQuery(id+"F0.wireOp",VERTEX,"E3.19.17.0");
            var Q23;
            Q23=sQuery(id+"F0.wireOp",VERTEX,"E3.19.9.0");
            var Q24;
            Q24=sQuery(id+"F0.wireOp",VERTEX,"E3.17.7.1");
            var Q25;
            Q25=sQuery(id+"F0.wireOp",VERTEX,"E3.19.1.1");
            var Q26;
            Q26=sQuery(id+"F0.wireOp",VERTEX,"E3.18.12.1");
            var Q27;
            Q27=sQuery(id+"F0.wireOp",VERTEX,"E3.18.4.1");
            var Q28;
            Q28=sQuery(id+"F0.wireOp",VERTEX,"E3.17.15.1");
            var Q29;
            Q29=sQuery(id+"F0.wireOp",VERTEX,"E3.19.17.1");
            var Q30;
            Q30=sQuery(id+"F0.wireOp",VERTEX,"E3.19.9.1");
            var Q31;
            Q31=sQuery(id+"F0.wireOp",VERTEX,"E3.19.2.0");
            var Q32;
            Q32=sQuery(id+"F0.wireOp",VERTEX,"E3.18.13.0");
            var Q33;
            Q33=sQuery(id+"F0.wireOp",VERTEX,"E3.18.5.0");
            var Q34;
            Q34=sQuery(id+"F0.wireOp",VERTEX,"E3.19.18.0");
            var Q35;
            Q35=sQuery(id+"F0.wireOp",VERTEX,"E3.19.10.0");
            var Q36;
            Q36=sQuery(id+"F0.wireOp",VERTEX,"E3.19.2.1");
            var Q37;
            Q37=sQuery(id+"F0.wireOp",VERTEX,"E3.18.13.1");
            var Q38;
            Q38=sQuery(id+"F0.wireOp",VERTEX,"E3.18.5.1");
            var Q39;
            Q39=sQuery(id+"F0.wireOp",VERTEX,"E3.17.16.1");
            var Q40;
            Q40=sQuery(id+"F0.wireOp",VERTEX,"E3.19.18.1");
            var Q41;
            Q41=sQuery(id+"F0.wireOp",VERTEX,"E3.19.10.1");
            var Q42;
            Q42=sQuery(id+"F0.wireOp",VERTEX,"E3.17.8.1");
            var Q43;
            Q43=sQuery(id+"F0.wireOp",VERTEX,"E3.17.0.1");
            var Q44;
            Q44=sQuery(id+"F0.wireOp",VERTEX,"E3.19.11.0");
            var Q45;
            Q45=sQuery(id+"F0.wireOp",VERTEX,"E3.19.3.0");
            var Q46;
            Q46=sQuery(id+"F0.wireOp",VERTEX,"E3.18.14.0");
            var Q47;
            Q47=sQuery(id+"F0.wireOp",VERTEX,"E3.18.6.0");
            var Q48;
            Q48=sQuery(id+"F0.wireOp",VERTEX,"E3.17.9.1");
            var Q49;
            Q49=sQuery(id+"F0.wireOp",VERTEX,"E3.17.1.1");
            var Q50;
            Q50=sQuery(id+"F0.wireOp",VERTEX,"E3.19.3.1");
            var Q51;
            Q51=sQuery(id+"F0.wireOp",VERTEX,"E3.18.14.1");
            var Q52;
            Q52=sQuery(id+"F0.wireOp",VERTEX,"E3.18.6.1");
            var Q53;
            Q53=sQuery(id+"F0.wireOp",VERTEX,"E3.17.17.1");
            var Q54;
            Q54=sQuery(id+"F0.wireOp",VERTEX,"E3.19.11.1");
            var Q55;
            Q55=sQuery(id+"F0.wireOp",VERTEX,"E3.19.4.0");
            var Q56;
            Q56=sQuery(id+"F0.wireOp",VERTEX,"E3.18.15.0");
            var Q57;
            Q57=sQuery(id+"F0.wireOp",VERTEX,"E3.18.7.0");
            var Q58;
            Q58=sQuery(id+"F0.wireOp",VERTEX,"E3.19.12.0");
            var Q59;
            Q59=sQuery(id+"F0.wireOp",VERTEX,"E3.18.7.1");
            var Q60;
            Q60=sQuery(id+"F0.wireOp",VERTEX,"E3.17.18.1");
            var Q61;
            Q61=sQuery(id+"F0.wireOp",VERTEX,"E3.17.10.1");
            var Q62;
            Q62=sQuery(id+"F0.wireOp",VERTEX,"E3.17.2.1");
            var Q63;
            Q63=sQuery(id+"F0.wireOp",VERTEX,"E3.19.12.1");
            var Q64;
            Q64=sQuery(id+"F0.wireOp",VERTEX,"E3.19.4.1");
            var Q65;
            Q65=sQuery(id+"F0.wireOp",VERTEX,"E3.18.15.1");
            var Q66;
            Q66=sQuery(id+"F0.wireOp",VERTEX,"E3.18.8.0");
            var Q67;
            Q67=sQuery(id+"F0.wireOp",VERTEX,"E3.18.0.0");
            var Q68;
            Q68=sQuery(id+"F0.wireOp",VERTEX,"E3.19.13.0");
            var Q69;
            Q69=sQuery(id+"F0.wireOp",VERTEX,"E3.19.5.0");
            var Q70;
            Q70=sQuery(id+"F0.wireOp",VERTEX,"E3.18.16.0");
            var Q71;
            Q71=sQuery(id+"F0.wireOp",VERTEX,"E3.18.8.1");
            var Q72;
            Q72=sQuery(id+"F0.wireOp",VERTEX,"E3.18.0.1");
            var Q73;
            Q73=sQuery(id+"F0.wireOp",VERTEX,"E3.17.11.1");
            var Q74;
            Q74=sQuery(id+"F0.wireOp",VERTEX,"E3.17.3.1");
            var Q75;
            Q75=sQuery(id+"F0.wireOp",VERTEX,"E3.19.13.1");
            var Q76;
            Q76=sQuery(id+"F0.wireOp",VERTEX,"E3.19.5.1");
            var Q77;
            Q77=sQuery(id+"F0.wireOp",VERTEX,"E3.18.16.1");
            var Q78;
            Q78=sQuery(id+"F0.wireOp",VERTEX,"E3.18.9.0");
            var Q79;
            Q79=sQuery(id+"F0.wireOp",VERTEX,"E3.18.1.0");
            var Q80;
            Q80=sQuery(id+"F0.wireOp",VERTEX,"E3.19.14.0");
            var Q81;
            Q81=sQuery(id+"F0.wireOp",VERTEX,"E3.19.6.0");
            var Q82;
            Q82=sQuery(id+"F0.wireOp",VERTEX,"E3.18.17.0");
            var Q83;
            Q83=sQuery(id+"F0.wireOp",VERTEX,"E3.18.9.1");
            var Q84;
            Q84=sQuery(id+"F0.wireOp",VERTEX,"E3.18.1.1");
            var Q85;
            Q85=sQuery(id+"F0.wireOp",VERTEX,"E3.17.12.1");
            var Q86;
            Q86=sQuery(id+"F0.wireOp",VERTEX,"E3.17.4.1");
            var Q87;
            Q87=sQuery(id+"F0.wireOp",VERTEX,"E3.19.14.1");
            var Q88;
            Q88=sQuery(id+"F0.wireOp",VERTEX,"E3.19.6.1");
            var Q89;
            Q89=sQuery(id+"F0.wireOp",VERTEX,"E3.18.17.1");
            var Q90;
            Q90=sQuery(id+"F0.wireOp",VERTEX,"E3.18.10.0");
            var Q91;
            Q91=sQuery(id+"F0.wireOp",VERTEX,"E3.18.2.0");
            var Q92;
            Q92=sQuery(id+"F0.wireOp",VERTEX,"E3.19.15.0");
            var Q93;
            Q93=sQuery(id+"F0.wireOp",VERTEX,"E3.19.7.0");
            var Q94;
            Q94=sQuery(id+"F0.wireOp",VERTEX,"E3.18.18.0");
            var Q95;
            Q95=makeQuery(id+"F1.opExtrude","SWEPT_BODY",BODY,{"disambiguationData":[OSD([sQuery(id+"F0.wireOp",EDGE,"E0.bottom"),sQuery(id+"F0.wireOp",EDGE,"E0.top"),sQuery(id+"F0.wireOp",EDGE,"E0.left"),sQuery(id+"F0.wireOp",EDGE,"E0.right")])]});
            hole(context, id + "F9", {"style" : HoleStyle.SIMPLE, "endStyle" : HoleEndStyle.THROUGH, "oppositeDirection" : true, "holeDiameter" : 6.35 * mm, "tappedDepth" : 12.7 * mm, "tapClearance" : 3, "startFromSketch" : true, "locations" : qUnion([Q0, Q1, Q2, Q3, Q4, Q5, Q6, Q7, Q8, Q9, Q10, Q11, Q12, Q13, Q14, Q15, Q16, Q17, Q18, Q19, Q20, Q21, Q22, Q23, Q24, Q25, Q26, Q27, Q28, Q29, Q30, Q31, Q32, Q33, Q34, Q35, Q36, Q37, Q38, Q39, Q40, Q41, Q42, Q43, Q44, Q45, Q46, Q47, Q48, Q49, Q50, Q51, Q52, Q53, Q54, Q55, Q56, Q57, Q58, Q59, Q60, Q61, Q62, Q63, Q64, Q65, Q66, Q67, Q68, Q69, Q70, Q71, Q72, Q73, Q74, Q75, Q76, Q77, Q78, Q79, Q80, Q81, Q82, Q83, Q84, Q85, Q86, Q87, Q88, Q89, Q90, Q91, Q92, Q93, Q94]), "scope" : qUnion([Q95])});
        }
        {
            var Q0;
            Q0=sQuery(id+"F0.wireOp",VERTEX,"E3.21.17.1");
            var Q1;
            Q1=sQuery(id+"F0.wireOp",VERTEX,"E3.20.12.1");
            var Q2;
            Q2=sQuery(id+"F0.wireOp",VERTEX,"E3.20.4.1");
            var Q3;
            Q3=sQuery(id+"F0.wireOp",VERTEX,"E3.21.9.1");
            var Q4;
            Q4=sQuery(id+"F0.wireOp",VERTEX,"E3.21.1.1");
            var Q5;
            Q5=sQuery(id+"F0.wireOp",VERTEX,"E3.21.18.0");
            var Q6;
            Q6=sQuery(id+"F0.wireOp",VERTEX,"E3.22.15.0");
            var Q7;
            Q7=sQuery(id+"F0.wireOp",VERTEX,"E3.22.7.0");
            var Q8;
            Q8=sQuery(id+"F0.wireOp",VERTEX,"E3.21.10.0");
            var Q9;
            Q9=sQuery(id+"F0.wireOp",VERTEX,"E3.21.2.0");
            var Q10;
            Q10=sQuery(id+"F0.wireOp",VERTEX,"E3.20.13.0");
            var Q11;
            Q11=sQuery(id+"F0.wireOp",VERTEX,"E3.20.5.0");
            var Q12;
            Q12=sQuery(id+"F0.wireOp",VERTEX,"E3.21.18.1");
            var Q13;
            Q13=sQuery(id+"F0.wireOp",VERTEX,"E3.20.13.1");
            var Q14;
            Q14=sQuery(id+"F0.wireOp",VERTEX,"E3.20.5.1");
            var Q15;
            Q15=sQuery(id+"F0.wireOp",VERTEX,"E3.21.10.1");
            var Q16;
            Q16=sQuery(id+"F0.wireOp",VERTEX,"E3.21.2.1");
            var Q17;
            Q17=sQuery(id+"F0.wireOp",VERTEX,"E3.22.0.0");
            var Q18;
            Q18=sQuery(id+"F0.wireOp",VERTEX,"E3.21.11.0");
            var Q19;
            Q19=sQuery(id+"F0.wireOp",VERTEX,"E3.22.16.0");
            var Q20;
            Q20=sQuery(id+"F0.wireOp",VERTEX,"E3.22.8.0");
            var Q21;
            Q21=sQuery(id+"F0.wireOp",VERTEX,"E3.20.14.0");
            var Q22;
            Q22=sQuery(id+"F0.wireOp",VERTEX,"E3.20.6.0");
            var Q23;
            Q23=sQuery(id+"F0.wireOp",VERTEX,"E3.21.3.0");
            var Q24;
            Q24=sQuery(id+"F0.wireOp",VERTEX,"E3.21.11.1");
            var Q25;
            Q25=sQuery(id+"F0.wireOp",VERTEX,"E3.20.14.1");
            var Q26;
            Q26=sQuery(id+"F0.wireOp",VERTEX,"E3.20.6.1");
            var Q27;
            Q27=sQuery(id+"F0.wireOp",VERTEX,"E3.21.3.1");
            var Q28;
            Q28=sQuery(id+"F0.wireOp",VERTEX,"E3.22.1.0");
            var Q29;
            Q29=sQuery(id+"F0.wireOp",VERTEX,"E3.21.12.0");
            var Q30;
            Q30=sQuery(id+"F0.wireOp",VERTEX,"E3.22.17.0");
            var Q31;
            Q31=sQuery(id+"F0.wireOp",VERTEX,"E3.22.9.0");
            var Q32;
            Q32=sQuery(id+"F0.wireOp",VERTEX,"E3.20.15.0");
            var Q33;
            Q33=sQuery(id+"F0.wireOp",VERTEX,"E3.20.7.0");
            var Q34;
            Q34=sQuery(id+"F0.wireOp",VERTEX,"E3.21.4.0");
            var Q35;
            Q35=sQuery(id+"F0.wireOp",VERTEX,"E3.21.12.1");
            var Q36;
            Q36=sQuery(id+"F0.wireOp",VERTEX,"E3.20.15.1");
            var Q37;
            Q37=sQuery(id+"F0.wireOp",VERTEX,"E3.20.7.1");
            var Q38;
            Q38=sQuery(id+"F0.wireOp",VERTEX,"E3.21.4.1");
            var Q39;
            Q39=sQuery(id+"F0.wireOp",VERTEX,"E3.22.2.0");
            var Q40;
            Q40=sQuery(id+"F0.wireOp",VERTEX,"E3.21.13.0");
            var Q41;
            Q41=sQuery(id+"F0.wireOp",VERTEX,"E3.22.18.0");
            var Q42;
            Q42=sQuery(id+"F0.wireOp",VERTEX,"E3.22.10.0");
            var Q43;
            Q43=sQuery(id+"F0.wireOp",VERTEX,"E3.20.16.0");
            var Q44;
            Q44=sQuery(id+"F0.wireOp",VERTEX,"E3.20.8.0");
            var Q45;
            Q45=sQuery(id+"F0.wireOp",VERTEX,"E3.20.0.0");
            var Q46;
            Q46=sQuery(id+"F0.wireOp",VERTEX,"E3.21.5.0");
            var Q47;
            Q47=sQuery(id+"F0.wireOp",VERTEX,"E3.21.13.1");
            var Q48;
            Q48=sQuery(id+"F0.wireOp",VERTEX,"E3.21.5.1");
            var Q49;
            Q49=sQuery(id+"F0.wireOp",VERTEX,"E3.20.16.1");
            var Q50;
            Q50=sQuery(id+"F0.wireOp",VERTEX,"E3.20.8.1");
            var Q51;
            Q51=sQuery(id+"F0.wireOp",VERTEX,"E3.20.0.1");
            var Q52;
            Q52=sQuery(id+"F0.wireOp",VERTEX,"E3.22.3.0");
            var Q53;
            Q53=sQuery(id+"F0.wireOp",VERTEX,"E3.21.14.0");
            var Q54;
            Q54=sQuery(id+"F0.wireOp",VERTEX,"E3.22.11.0");
            var Q55;
            Q55=sQuery(id+"F0.wireOp",VERTEX,"E3.20.17.0");
            var Q56;
            Q56=sQuery(id+"F0.wireOp",VERTEX,"E3.20.9.0");
            var Q57;
            Q57=sQuery(id+"F0.wireOp",VERTEX,"E3.20.1.0");
            var Q58;
            Q58=sQuery(id+"F0.wireOp",VERTEX,"E3.21.6.0");
            var Q59;
            Q59=sQuery(id+"F0.wireOp",VERTEX,"E3.21.14.1");
            var Q60;
            Q60=sQuery(id+"F0.wireOp",VERTEX,"E3.20.1.1");
            var Q61;
            Q61=sQuery(id+"F0.wireOp",VERTEX,"E3.21.6.1");
            var Q62;
            Q62=sQuery(id+"F0.wireOp",VERTEX,"E3.20.17.1");
            var Q63;
            Q63=sQuery(id+"F0.wireOp",VERTEX,"E3.20.9.1");
            var Q64;
            Q64=sQuery(id+"F0.wireOp",VERTEX,"E3.22.12.0");
            var Q65;
            Q65=sQuery(id+"F0.wireOp",VERTEX,"E3.22.4.0");
            var Q66;
            Q66=sQuery(id+"F0.wireOp",VERTEX,"E3.21.15.0");
            var Q67;
            Q67=sQuery(id+"F0.wireOp",VERTEX,"E3.20.2.0");
            var Q68;
            Q68=sQuery(id+"F0.wireOp",VERTEX,"E3.21.7.0");
            var Q69;
            Q69=sQuery(id+"F0.wireOp",VERTEX,"E3.20.18.0");
            var Q70;
            Q70=sQuery(id+"F0.wireOp",VERTEX,"E3.20.10.0");
            var Q71;
            Q71=sQuery(id+"F0.wireOp",VERTEX,"E3.21.15.1");
            var Q72;
            Q72=sQuery(id+"F0.wireOp",VERTEX,"E3.22.13.0");
            var Q73;
            Q73=sQuery(id+"F0.wireOp",VERTEX,"E3.22.5.0");
            var Q74;
            Q74=sQuery(id+"F0.wireOp",VERTEX,"E3.21.16.0");
            var Q75;
            Q75=sQuery(id+"F0.wireOp",VERTEX,"E3.20.2.1");
            var Q76;
            Q76=sQuery(id+"F0.wireOp",VERTEX,"E3.21.7.1");
            var Q77;
            Q77=sQuery(id+"F0.wireOp",VERTEX,"E3.20.18.1");
            var Q78;
            Q78=sQuery(id+"F0.wireOp",VERTEX,"E3.20.10.1");
            var Q79;
            Q79=sQuery(id+"F0.wireOp",VERTEX,"E3.21.16.1");
            var Q80;
            Q80=sQuery(id+"F0.wireOp",VERTEX,"E3.20.3.0");
            var Q81;
            Q81=sQuery(id+"F0.wireOp",VERTEX,"E3.21.8.0");
            var Q82;
            Q82=sQuery(id+"F0.wireOp",VERTEX,"E3.21.0.0");
            var Q83;
            Q83=sQuery(id+"F0.wireOp",VERTEX,"E3.20.11.0");
            var Q84;
            Q84=sQuery(id+"F0.wireOp",VERTEX,"E3.20.3.1");
            var Q85;
            Q85=sQuery(id+"F0.wireOp",VERTEX,"E3.22.14.0");
            var Q86;
            Q86=sQuery(id+"F0.wireOp",VERTEX,"E3.22.6.0");
            var Q87;
            Q87=sQuery(id+"F0.wireOp",VERTEX,"E3.21.17.0");
            var Q88;
            Q88=sQuery(id+"F0.wireOp",VERTEX,"E3.21.8.1");
            var Q89;
            Q89=sQuery(id+"F0.wireOp",VERTEX,"E3.21.0.1");
            var Q90;
            Q90=sQuery(id+"F0.wireOp",VERTEX,"E3.20.11.1");
            var Q91;
            Q91=sQuery(id+"F0.wireOp",VERTEX,"E3.20.4.0");
            var Q92;
            Q92=sQuery(id+"F0.wireOp",VERTEX,"E3.21.9.0");
            var Q93;
            Q93=sQuery(id+"F0.wireOp",VERTEX,"E3.21.1.0");
            var Q94;
            Q94=sQuery(id+"F0.wireOp",VERTEX,"E3.20.12.0");
            var Q95;
            Q95=makeQuery(id+"F1.opExtrude","SWEPT_BODY",BODY,{"disambiguationData":[OSD([sQuery(id+"F0.wireOp",EDGE,"E0.bottom"),sQuery(id+"F0.wireOp",EDGE,"E0.top"),sQuery(id+"F0.wireOp",EDGE,"E0.left"),sQuery(id+"F0.wireOp",EDGE,"E0.right")])]});
            hole(context, id + "F10", {"style" : HoleStyle.SIMPLE, "endStyle" : HoleEndStyle.THROUGH, "oppositeDirection" : true, "holeDiameter" : 6.35 * mm, "tappedDepth" : 12.7 * mm, "tapClearance" : 3, "startFromSketch" : true, "locations" : qUnion([Q0, Q1, Q2, Q3, Q4, Q5, Q6, Q7, Q8, Q9, Q10, Q11, Q12, Q13, Q14, Q15, Q16, Q17, Q18, Q19, Q20, Q21, Q22, Q23, Q24, Q25, Q26, Q27, Q28, Q29, Q30, Q31, Q32, Q33, Q34, Q35, Q36, Q37, Q38, Q39, Q40, Q41, Q42, Q43, Q44, Q45, Q46, Q47, Q48, Q49, Q50, Q51, Q52, Q53, Q54, Q55, Q56, Q57, Q58, Q59, Q60, Q61, Q62, Q63, Q64, Q65, Q66, Q67, Q68, Q69, Q70, Q71, Q72, Q73, Q74, Q75, Q76, Q77, Q78, Q79, Q80, Q81, Q82, Q83, Q84, Q85, Q86, Q87, Q88, Q89, Q90, Q91, Q92, Q93, Q94]), "scope" : qUnion([Q95])});
        }
        {
            var Q0;
            Q0=sQuery(id+"F0.wireOp",VERTEX,"E3.22.14.1");
            var Q1;
            Q1=sQuery(id+"F0.wireOp",VERTEX,"E3.22.6.1");
            var Q2;
            Q2=sQuery(id+"F0.wireOp",VERTEX,"E3.22.15.1");
            var Q3;
            Q3=sQuery(id+"F0.wireOp",VERTEX,"E3.22.7.1");
            var Q4;
            Q4=sQuery(id+"F0.wireOp",VERTEX,"E3.22.0.1");
            var Q5;
            Q5=sQuery(id+"F0.wireOp",VERTEX,"E3.22.16.1");
            var Q6;
            Q6=sQuery(id+"F0.wireOp",VERTEX,"E3.22.8.1");
            var Q7;
            Q7=sQuery(id+"F0.wireOp",VERTEX,"E3.22.17.1");
            var Q8;
            Q8=sQuery(id+"F0.wireOp",VERTEX,"E3.22.9.1");
            var Q9;
            Q9=sQuery(id+"F0.wireOp",VERTEX,"E3.22.1.1");
            var Q10;
            Q10=sQuery(id+"F0.wireOp",VERTEX,"E3.22.2.1");
            var Q11;
            Q11=sQuery(id+"F0.wireOp",VERTEX,"E3.22.10.1");
            var Q12;
            Q12=sQuery(id+"F0.wireOp",VERTEX,"E3.22.11.1");
            var Q13;
            Q13=sQuery(id+"F0.wireOp",VERTEX,"E3.22.3.1");
            var Q14;
            Q14=sQuery(id+"F0.wireOp",VERTEX,"E3.22.12.1");
            var Q15;
            Q15=sQuery(id+"F0.wireOp",VERTEX,"E3.22.4.1");
            var Q16;
            Q16=sQuery(id+"F0.wireOp",VERTEX,"E3.22.13.1");
            var Q17;
            Q17=sQuery(id+"F0.wireOp",VERTEX,"E3.22.5.1");
            var Q18;
            Q18=makeQuery(id+"F1.opExtrude","SWEPT_BODY",BODY,{"disambiguationData":[OSD([sQuery(id+"F0.wireOp",EDGE,"E0.bottom"),sQuery(id+"F0.wireOp",EDGE,"E0.top"),sQuery(id+"F0.wireOp",EDGE,"E0.left"),sQuery(id+"F0.wireOp",EDGE,"E0.right")])]});
            hole(context, id + "F11", {"style" : HoleStyle.SIMPLE, "endStyle" : HoleEndStyle.THROUGH, "oppositeDirection" : true, "holeDiameter" : 6.35 * mm, "tappedDepth" : 12.7 * mm, "tapClearance" : 3, "startFromSketch" : true, "locations" : qUnion([Q0, Q1, Q2, Q3, Q4, Q5, Q6, Q7, Q8, Q9, Q10, Q11, Q12, Q13, Q14, Q15, Q16, Q17]), "scope" : qUnion([Q18])});
        }
        {
            var Q0;
            Q0=sQuery(id+"F0.wireOp",VERTEX,"E1");
            var Q1;
            Q1=sQuery(id+"F0.wireOp",VERTEX,"E3.22.18.1");
            var Q2;
            Q2=makeQuery(id+"F1.opExtrude","SWEPT_BODY",BODY,{"disambiguationData":[OSD([sQuery(id+"F0.wireOp",EDGE,"E0.bottom"),sQuery(id+"F0.wireOp",EDGE,"E0.top"),sQuery(id+"F0.wireOp",EDGE,"E0.left"),sQuery(id+"F0.wireOp",EDGE,"E0.right")])]});
            hole(context, id + "F12", {"style" : HoleStyle.SIMPLE, "endStyle" : HoleEndStyle.THROUGH, "oppositeDirection" : true, "holeDiameter" : 6.35 * mm, "tappedDepth" : 12.7 * mm, "tapClearance" : 3, "startFromSketch" : true, "locations" : qUnion([Q0, Q1]), "scope" : qUnion([Q2])});
        }
    });
